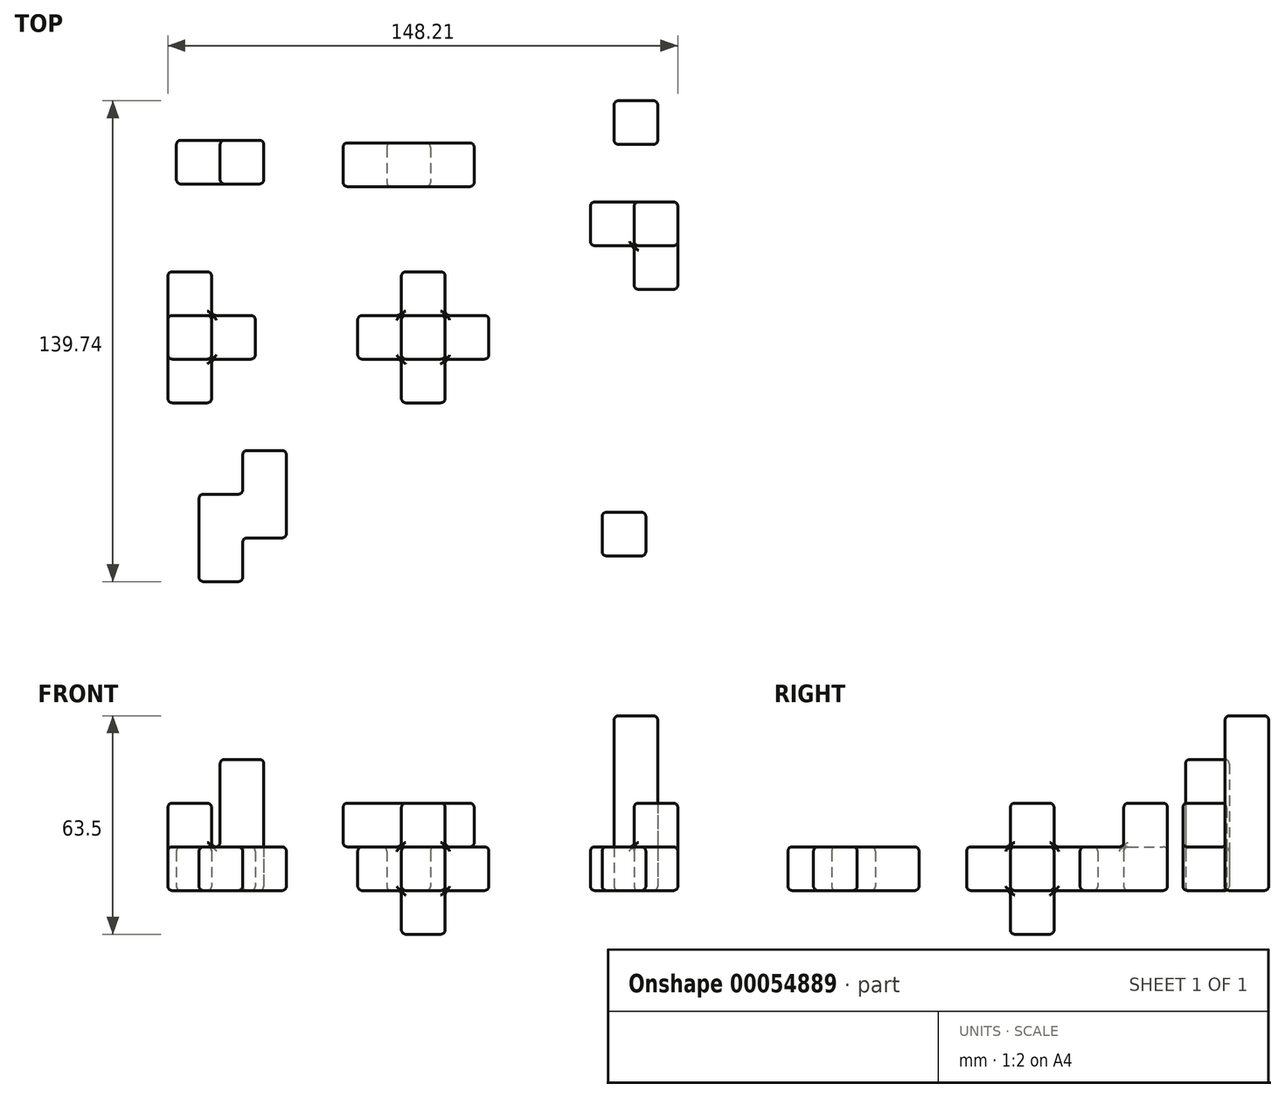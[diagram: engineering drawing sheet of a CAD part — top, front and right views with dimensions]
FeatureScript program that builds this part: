
annotation { "Feature Type Name" : "Feature", "Feature Type Description" : "" }
export const myFeature = defineFeature(function(context is Context, id is Id, definition is map)
    precondition{}
    {
        {
            var Q0;
            Q0=qCreatedBy(makeId("Top.planeOp"),FACE);
            var sketch = newSketch(context, id + "F0", { "sketchPlane" : qUnion([Q0])});
            skLineSegment(sketch, "E0.rect.bottom", {"start": v(6.35, 19.05) * mm, "end": v(-6.35, 19.05) * mm});
            skLineSegment(sketch, "E0.rect.top", {"start": v(6.35, -19.05) * mm, "end": v(-6.35, -19.05) * mm});
            skLineSegment(sketch, "E0.rect.left", {"start": v(6.35, 19.05) * mm, "end": v(6.35, -19.05) * mm});
            skLineSegment(sketch, "E0.rect.right", {"start": v(-6.35, 19.05) * mm, "end": v(-6.35, -19.05) * mm});
            skPoint(sketch, "E0.rect.middle", {"position": v(0, 0) * mm});
            skSolve(sketch);
        }
        {
            var Q0;
            Q0 = qSketchRegion(id + "F0", true);
            extrude(context, id + "F1", {"entities" : qUnion([Q0]), "depth" : 12.7 * mm});
        }
        {
            var Q0;
            Q0=makeQuery(id+"F1.opExtrude","CAP_FACE",FACE,{"disambiguationData":[OSD([sQuery(id+"F0.wireOp",EDGE,"E0.rect.bottom"),sQuery(id+"F0.wireOp",EDGE,"E0.rect.top"),sQuery(id+"F0.wireOp",EDGE,"E0.rect.left"),sQuery(id+"F0.wireOp",EDGE,"E0.rect.right")])],"isStart":false});
            var sketch = newSketch(context, id + "F2", { "sketchPlane" : qUnion([Q0])});
            skLineSegment(sketch, "E1.rect.bottom", {"start": v(6.35, 6.35) * mm, "end": v(-6.35, 6.35) * mm});
            skLineSegment(sketch, "E1.rect.top", {"start": v(6.35, -6.35) * mm, "end": v(-6.35, -6.35) * mm});
            skLineSegment(sketch, "E1.rect.left", {"start": v(6.35, 6.35) * mm, "end": v(6.35, -6.35) * mm});
            skLineSegment(sketch, "E1.rect.right", {"start": v(-6.35, 6.35) * mm, "end": v(-6.35, -6.35) * mm});
            skPoint(sketch, "E1.rect.middle", {"position": v(0, 0) * mm});
            skSolve(sketch);
        }
        {
            var Q0;
            Q0 = qSketchRegion(id + "F2", true);
            extrude(context, id + "F3", {"entities" : qUnion([Q0]), "operationType" : NewBodyOperationType.ADD, "depth" : 12.7 * mm});
        }
        {
            var Q0;
            Q0=makeQuery(id+"F3.boolean.opBoolean","MERGE",FACE,{"derivedFrom":[makeQuery(id+"F1.opExtrude","SWEPT_FACE",FACE,{"disambiguationData":[OSD([sQuery(id+"F0.wireOp",EDGE,"E0.rect.left")])]}),makeQuery(id+"F3.opExtrude","SWEPT_FACE",FACE,{"disambiguationData":[OSD([sQuery(id+"F2.wireOp",EDGE,"E1.rect.left")])]})]});
            var sketch = newSketch(context, id + "F4", { "sketchPlane" : qUnion([Q0])});
            skLineSegment(sketch, "E2.bottom", {"start": v(-6.35, 12.7) * mm, "end": v(6.35, 12.7) * mm});
            skLineSegment(sketch, "E2.top", {"start": v(-6.35, 0) * mm, "end": v(6.35, 0) * mm});
            skLineSegment(sketch, "E2.left", {"start": v(-6.35, 12.7) * mm, "end": v(-6.35, 0) * mm});
            skLineSegment(sketch, "E2.right", {"start": v(6.35, 12.7) * mm, "end": v(6.35, 0) * mm});
            skSolve(sketch);
        }
        {
            var Q0;
            Q0 = qSketchRegion(id + "F4", true);
            extrude(context, id + "F5", {"entities" : qUnion([Q0]), "operationType" : NewBodyOperationType.ADD, "depth" : 12.7 * mm});
        }
        {
            var Q0;
            Q0 = qSketchRegion(id + "F4", true);
            extrude(context, id + "F6", {"entities" : qUnion([Q0]), "operationType" : NewBodyOperationType.ADD, "oppositeDirection" : true, "depth" : 25.4 * mm});
        }
        {
            var Q0;
            Q0 = qSketchRegion(id + "F2", true);
            extrude(context, id + "F7", {"entities" : qUnion([Q0]), "operationType" : NewBodyOperationType.ADD, "oppositeDirection" : true, "depth" : 25.4 * mm});
        }
        {
            var Q0;
            Q0=makeQuery(id+"F1.opExtrude","SWEPT_FACE",FACE,{"disambiguationData":[OSD([sQuery(id+"F0.wireOp",EDGE,"E0.rect.bottom")])]});
            var Q1;
            Q1=makeQuery(id+"F1.opExtrude","SWEPT_EDGE",EDGE,{"disambiguationData":[OSD([sQuery(id+"F0.wireOp",EDGE,"E0.rect.bottom"),sQuery(id+"F0.wireOp",EDGE,"E0.rect.left")])]});
            var Q2;
            Q2=makeQuery(id+"F5.opExtrude","SWEPT_FACE",FACE,{"disambiguationData":[OSD([sQuery(id+"F4.wireOp",EDGE,"E2.bottom")])]});
            var Q3;
            Q3=makeQuery(id+"F1.opExtrude","SWEPT_FACE",FACE,{"disambiguationData":[OSD([sQuery(id+"F0.wireOp",EDGE,"E0.rect.top")])]});
            var Q4;
            Q4=makeQuery(id+"F1.opExtrude","CAP_EDGE",EDGE,{"disambiguationData":[OSD([sQuery(id+"F0.wireOp",EDGE,"E0.rect.bottom")])],"isStart":true});
            var Q5;
            Q5=makeQuery(id+"F3.opExtrude","CAP_EDGE",EDGE,{"disambiguationData":[OSD([sQuery(id+"F2.wireOp",EDGE,"E1.rect.top")])],"isStart":false});
            var Q6;
            Q6=makeQuery(id+"F1.opExtrude","CAP_EDGE",EDGE,{"disambiguationData":[OSD([sQuery(id+"F0.wireOp",EDGE,"E0.rect.bottom")])],"isStart":false});
            var Q7;
            Q7=makeQuery(id+"F1.opExtrude","CAP_EDGE",EDGE,{"disambiguationData":[OSD([sQuery(id+"F0.wireOp",EDGE,"E0.rect.top")])],"isStart":false});
            var Q8;
            Q8=makeQuery(id+"F5.opExtrude","SWEPT_EDGE",EDGE,{"disambiguationData":[OSD([sQuery(id+"F0.wireOp",EDGE,"E0.rect.left"),sQuery(id+"F2.wireOp",EDGE,"E1.rect.bottom"),sQuery(id+"F2.wireOp",EDGE,"E1.rect.left"),sQuery(id+"F4.wireOp",EDGE,"E2.bottom"),sQuery(id+"F4.wireOp",EDGE,"E2.right")])]});
            var Q9;
            Q9=makeQuery(id+"F3.opExtrude","CAP_EDGE",EDGE,{"disambiguationData":[OSD([sQuery(id+"F2.wireOp",EDGE,"E1.rect.bottom")])],"isStart":true});
            var Q10;
            Q10=makeQuery(id+"F7.opExtrude","CAP_EDGE",EDGE,{"disambiguationData":[OSD([sQuery(id+"F2.wireOp",EDGE,"E1.rect.bottom")])],"isStart":false});
            var Q11;
            Q11=makeQuery(id+"F5.opExtrude","SWEPT_EDGE",EDGE,{"disambiguationData":[OSD([sQuery(id+"F0.wireOp",EDGE,"E0.rect.left"),sQuery(id+"F2.wireOp",EDGE,"E1.rect.top"),sQuery(id+"F2.wireOp",EDGE,"E1.rect.left"),sQuery(id+"F4.wireOp",EDGE,"E2.bottom"),sQuery(id+"F4.wireOp",EDGE,"E2.left")])]});
            var Q12;
            {var subQ0=sQuery(id+"F0.wireOp",EDGE,"E0.rect.right");var subQ1=sQuery(id+"F0.wireOp",EDGE,"E0.rect.left");var subQ2=sQuery(id+"F0.wireOp",EDGE,"E0.rect.bottom");Q12=makeQuery(id+"F3.boolean.opBoolean","SPLIT",FACE,{"disambiguationData":[TD([makeQuery(id+"F1.opExtrude","SWEPT_FACE",FACE,{"disambiguationData":[OSD([subQ2])]})])],"derivedFrom":makeQuery(id+"F1.opExtrude","CAP_FACE",FACE,{"disambiguationData":[OSD([subQ2,sQuery(id+"F0.wireOp",EDGE,"E0.rect.top"),subQ1,subQ0])],"isStart":false})});}
            var Q13;
            {var subQ0=sQuery(id+"F0.wireOp",EDGE,"E0.rect.left");var subQ1=sQuery(id+"F0.wireOp",EDGE,"E0.rect.bottom");Q13=makeQuery(id+"F3.boolean.opBoolean","SPLIT",EDGE,{"disambiguationData":[TD([makeQuery(id+"F1.opExtrude","SWEPT_FACE",FACE,{"disambiguationData":[OSD([subQ1])]})])],"derivedFrom":makeQuery(id+"F1.opExtrude","CAP_EDGE",EDGE,{"disambiguationData":[OSD([subQ0])],"isStart":false})});}
            var Q14;
            Q14=makeQuery(id+"F3.opExtrude","CAP_EDGE",EDGE,{"disambiguationData":[OSD([sQuery(id+"F2.wireOp",EDGE,"E1.rect.left")])],"isStart":false});
            var Q15;
            {var subQ0=sQuery(id+"F0.wireOp",EDGE,"E0.rect.right");var subQ1=sQuery(id+"F0.wireOp",EDGE,"E0.rect.left");var subQ2=sQuery(id+"F0.wireOp",EDGE,"E0.rect.top");Q15=makeQuery(id+"F3.boolean.opBoolean","SPLIT",FACE,{"disambiguationData":[TD([makeQuery(id+"F1.opExtrude","SWEPT_FACE",FACE,{"disambiguationData":[OSD([subQ2])]})])],"derivedFrom":makeQuery(id+"F1.opExtrude","CAP_FACE",FACE,{"disambiguationData":[OSD([sQuery(id+"F0.wireOp",EDGE,"E0.rect.bottom"),subQ2,subQ1,subQ0])],"isStart":false})});}
            var Q16;
            {var subQ0=sQuery(id+"F0.wireOp",EDGE,"E0.rect.right");var subQ1=sQuery(id+"F0.wireOp",EDGE,"E0.rect.bottom");Q16=makeQuery(id+"F3.boolean.opBoolean","SPLIT",EDGE,{"disambiguationData":[TD([makeQuery(id+"F1.opExtrude","SWEPT_FACE",FACE,{"disambiguationData":[OSD([subQ1])]})])],"derivedFrom":makeQuery(id+"F1.opExtrude","CAP_EDGE",EDGE,{"disambiguationData":[OSD([subQ0])],"isStart":false})});}
            var Q17;
            Q17=makeQuery(id+"F3.opExtrude","CAP_EDGE",EDGE,{"disambiguationData":[OSD([sQuery(id+"F2.wireOp",EDGE,"E1.rect.right")])],"isStart":false});
            var Q18;
            Q18=makeQuery(id+"F3.opExtrude","SWEPT_FACE",FACE,{"disambiguationData":[OSD([sQuery(id+"F2.wireOp",EDGE,"E1.rect.bottom")])]});
            var Q19;
            Q19=makeQuery(id+"F5.opExtrude","SWEPT_EDGE",EDGE,{"disambiguationData":[OSD([sQuery(id+"F0.wireOp",EDGE,"E0.rect.left"),sQuery(id+"F4.wireOp",EDGE,"E2.top"),sQuery(id+"F4.wireOp",EDGE,"E2.right")])]});
            var Q20;
            Q20=makeQuery(id+"F3.opExtrude","SWEPT_EDGE",EDGE,{"disambiguationData":[OSD([sQuery(id+"F0.wireOp",EDGE,"E0.rect.right"),sQuery(id+"F2.wireOp",EDGE,"E1.rect.bottom"),sQuery(id+"F2.wireOp",EDGE,"E1.rect.right")])]});
            var Q21;
            Q21=makeQuery(id+"F3.opExtrude","CAP_FACE",FACE,{"disambiguationData":[OSD([sQuery(id+"F2.wireOp",EDGE,"E1.rect.bottom"),sQuery(id+"F2.wireOp",EDGE,"E1.rect.top"),sQuery(id+"F2.wireOp",EDGE,"E1.rect.left"),sQuery(id+"F2.wireOp",EDGE,"E1.rect.right")])],"isStart":false});
            var Q22;
            Q22=makeQuery(id+"F3.opExtrude","SWEPT_FACE",FACE,{"disambiguationData":[OSD([sQuery(id+"F2.wireOp",EDGE,"E1.rect.top")])]});
            var Q23;
            Q23=makeQuery(id+"F3.opExtrude","CAP_EDGE",EDGE,{"disambiguationData":[OSD([sQuery(id+"F2.wireOp",EDGE,"E1.rect.bottom")])],"isStart":false});
            var Q24;
            Q24=makeQuery(id+"F5.opExtrude","CAP_FACE",FACE,{"disambiguationData":[OSD([sQuery(id+"F4.wireOp",EDGE,"E2.bottom"),sQuery(id+"F4.wireOp",EDGE,"E2.top"),sQuery(id+"F4.wireOp",EDGE,"E2.left"),sQuery(id+"F4.wireOp",EDGE,"E2.right")])],"isStart":false});
            var Q25;
            Q25=makeQuery(id+"F5.opExtrude","SWEPT_FACE",FACE,{"disambiguationData":[OSD([sQuery(id+"F4.wireOp",EDGE,"E2.left")])]});
            var Q26;
            Q26=makeQuery(id+"F5.opExtrude","CAP_EDGE",EDGE,{"disambiguationData":[OSD([sQuery(id+"F4.wireOp",EDGE,"E2.bottom")])],"isStart":false});
            var Q27;
            Q27=makeQuery(id+"F5.opExtrude","SWEPT_FACE",FACE,{"disambiguationData":[OSD([sQuery(id+"F4.wireOp",EDGE,"E2.right")])]});
            var Q28;
            Q28=makeQuery(id+"F5.opExtrude","CAP_EDGE",EDGE,{"disambiguationData":[OSD([sQuery(id+"F4.wireOp",EDGE,"E2.bottom")])],"isStart":true});
            var Q29;
            Q29=makeQuery(id+"F5.opExtrude","CAP_EDGE",EDGE,{"disambiguationData":[OSD([sQuery(id+"F4.wireOp",EDGE,"E2.top")])],"isStart":false});
            var Q30;
            {var subQ0=sQuery(id+"F2.wireOp",EDGE,"E1.rect.left");var subQ1=sQuery(id+"F2.wireOp",EDGE,"E1.rect.top");var subQ2=sQuery(id+"F2.wireOp",EDGE,"E1.rect.bottom");var subQ3=sQuery(id+"F0.wireOp",EDGE,"E0.rect.left");var subQ4=makeQuery(id+"F1.opExtrude","SWEPT_FACE",FACE,{"disambiguationData":[OSD([subQ3])]});var subQ5=makeQuery(id+"F3.opExtrude","SWEPT_FACE",FACE,{"disambiguationData":[OSD([subQ0])]});Q30=makeQuery(id+"F5.boolean.opBoolean","SPLIT",FACE,{"disambiguationData":[TD([makeQuery(id+"F3.opExtrude","CAP_FACE",FACE,{"disambiguationData":[OSD([subQ2,subQ1,subQ0,sQuery(id+"F2.wireOp",EDGE,"E1.rect.right")])],"isStart":false})])],"derivedFrom":makeQuery(id+"F3.boolean.opBoolean","MERGE",FACE,{"derivedFrom":[subQ4,subQ5]})});}
            var Q31;
            {var subQ0=sQuery(id+"F0.wireOp",EDGE,"E0.rect.left");var subQ1=makeQuery(id+"F1.opExtrude","SWEPT_FACE",FACE,{"disambiguationData":[OSD([subQ0])]});var subQ4=sQuery(id+"F0.wireOp",EDGE,"E0.rect.bottom");var subQ5=makeQuery(id+"F3.opExtrude","SWEPT_FACE",FACE,{"disambiguationData":[OSD([sQuery(id+"F2.wireOp",EDGE,"E1.rect.left")])]});Q31=makeQuery(id+"F5.boolean.opBoolean","SPLIT",FACE,{"disambiguationData":[TD([makeQuery(id+"F1.opExtrude","SWEPT_FACE",FACE,{"disambiguationData":[OSD([subQ4])]})])],"derivedFrom":makeQuery(id+"F3.boolean.opBoolean","MERGE",FACE,{"derivedFrom":[subQ1,subQ5]})});}
            var Q32;
            Q32=makeQuery(id+"F7.opExtrude","CAP_FACE",FACE,{"disambiguationData":[OSD([sQuery(id+"F2.wireOp",EDGE,"E1.rect.bottom"),sQuery(id+"F2.wireOp",EDGE,"E1.rect.top"),sQuery(id+"F2.wireOp",EDGE,"E1.rect.left"),sQuery(id+"F2.wireOp",EDGE,"E1.rect.right")])],"isStart":false});
            var Q33;
            {var subQ0=sQuery(id+"F0.wireOp",EDGE,"E0.rect.left");var subQ1=makeQuery(id+"F1.opExtrude","SWEPT_FACE",FACE,{"disambiguationData":[OSD([subQ0])]});var subQ2=sQuery(id+"F0.wireOp",EDGE,"E0.rect.top");var subQ5=makeQuery(id+"F3.opExtrude","SWEPT_FACE",FACE,{"disambiguationData":[OSD([sQuery(id+"F2.wireOp",EDGE,"E1.rect.left")])]});Q33=makeQuery(id+"F5.boolean.opBoolean","SPLIT",FACE,{"disambiguationData":[TD([makeQuery(id+"F1.opExtrude","SWEPT_FACE",FACE,{"disambiguationData":[OSD([subQ2])]})])],"derivedFrom":makeQuery(id+"F3.boolean.opBoolean","MERGE",FACE,{"derivedFrom":[subQ1,subQ5]})});}
            var Q34;
            {var subQ0=sQuery(id+"F0.wireOp",EDGE,"E0.rect.left");var subQ1=sQuery(id+"F0.wireOp",EDGE,"E0.rect.bottom");Q34=makeQuery(id+"F5.boolean.opBoolean","SPLIT",EDGE,{"disambiguationData":[TD([makeQuery(id+"F1.opExtrude","SWEPT_FACE",FACE,{"disambiguationData":[OSD([subQ1])]})])],"derivedFrom":makeQuery(id+"F1.opExtrude","CAP_EDGE",EDGE,{"disambiguationData":[OSD([subQ0])],"isStart":true})});}
            var Q35;
            {var subQ0=sQuery(id+"F0.wireOp",EDGE,"E0.rect.left");var subQ1=sQuery(id+"F0.wireOp",EDGE,"E0.rect.top");Q35=makeQuery(id+"F5.boolean.opBoolean","SPLIT",EDGE,{"disambiguationData":[TD([makeQuery(id+"F1.opExtrude","SWEPT_FACE",FACE,{"disambiguationData":[OSD([subQ1])]})])],"derivedFrom":makeQuery(id+"F1.opExtrude","CAP_EDGE",EDGE,{"disambiguationData":[OSD([subQ0])],"isStart":true})});}
            var Q36;
            Q36=makeQuery(id+"F6.opExtrude","SWEPT_FACE",FACE,{"disambiguationData":[OSD([sQuery(id+"F4.wireOp",EDGE,"E2.right")])]});
            var Q37;
            Q37=makeQuery(id+"F6.opExtrude","CAP_EDGE",EDGE,{"disambiguationData":[OSD([sQuery(id+"F4.wireOp",EDGE,"E2.right")])],"isStart":false});
            var Q38;
            {var subQ0=sQuery(id+"F0.wireOp",EDGE,"E0.rect.right");var subQ1=makeQuery(id+"F1.opExtrude","SWEPT_FACE",FACE,{"disambiguationData":[OSD([subQ0])]});var subQ4=sQuery(id+"F0.wireOp",EDGE,"E0.rect.bottom");var subQ5=makeQuery(id+"F3.opExtrude","SWEPT_FACE",FACE,{"disambiguationData":[OSD([sQuery(id+"F2.wireOp",EDGE,"E1.rect.right")])]});Q38=makeQuery(id+"F6.boolean.opBoolean","SPLIT",FACE,{"disambiguationData":[TD([makeQuery(id+"F1.opExtrude","SWEPT_FACE",FACE,{"disambiguationData":[OSD([subQ4])]})])],"derivedFrom":makeQuery(id+"F3.boolean.opBoolean","MERGE",FACE,{"derivedFrom":[subQ1,subQ5]})});}
            var Q39;
            Q39=makeQuery(id+"F6.opExtrude","CAP_FACE",FACE,{"disambiguationData":[OSD([sQuery(id+"F4.wireOp",EDGE,"E2.bottom"),sQuery(id+"F4.wireOp",EDGE,"E2.top"),sQuery(id+"F4.wireOp",EDGE,"E2.left"),sQuery(id+"F4.wireOp",EDGE,"E2.right")])],"isStart":false});
            var Q40;
            Q40=makeQuery(id+"F6.opExtrude","SWEPT_EDGE",EDGE,{"disambiguationData":[OSD([sQuery(id+"F0.wireOp",EDGE,"E0.rect.left"),sQuery(id+"F2.wireOp",EDGE,"E1.rect.bottom"),sQuery(id+"F2.wireOp",EDGE,"E1.rect.left"),sQuery(id+"F4.wireOp",EDGE,"E2.bottom"),sQuery(id+"F4.wireOp",EDGE,"E2.right")])]});
            var Q41;
            Q41=makeQuery(id+"F6.opExtrude","SWEPT_FACE",FACE,{"disambiguationData":[OSD([sQuery(id+"F4.wireOp",EDGE,"E2.bottom")])]});
            var Q42;
            Q42=makeQuery(id+"F7.opExtrude","SWEPT_FACE",FACE,{"disambiguationData":[OSD([sQuery(id+"F2.wireOp",EDGE,"E1.rect.bottom")])]});
            var Q43;
            Q43=makeQuery(id+"F7.opExtrude","SWEPT_FACE",FACE,{"disambiguationData":[OSD([sQuery(id+"F2.wireOp",EDGE,"E1.rect.top")])]});
            var Q44;
            Q44=makeQuery(id+"F7.opExtrude","SWEPT_EDGE",EDGE,{"disambiguationData":[OSD([sQuery(id+"F0.wireOp",EDGE,"E0.rect.right"),sQuery(id+"F2.wireOp",EDGE,"E1.rect.bottom"),sQuery(id+"F2.wireOp",EDGE,"E1.rect.right")])]});
            var Q45;
            Q45=makeQuery(id+"F7.opExtrude","SWEPT_FACE",FACE,{"disambiguationData":[OSD([sQuery(id+"F2.wireOp",EDGE,"E1.rect.left")])]});
            var Q46;
            Q46=makeQuery(id+"F7.opExtrude","CAP_EDGE",EDGE,{"disambiguationData":[OSD([sQuery(id+"F2.wireOp",EDGE,"E1.rect.left")])],"isStart":false});
            var Q47;
            {var subQ0=sQuery(id+"F4.wireOp",EDGE,"E2.top");var subQ1=makeQuery(id+"F6.opExtrude","SWEPT_FACE",FACE,{"disambiguationData":[OSD([subQ0])]});var subQ2=makeQuery(id+"F5.opExtrude","SWEPT_FACE",FACE,{"disambiguationData":[OSD([subQ0])]});var subQ4=sQuery(id+"F0.wireOp",EDGE,"E0.rect.left");var subQ5=sQuery(id+"F0.wireOp",EDGE,"E0.rect.bottom");var subQ7=sQuery(id+"F0.wireOp",EDGE,"E0.rect.right");var subQ8=makeQuery(id+"F1.opExtrude","CAP_FACE",FACE,{"disambiguationData":[OSD([subQ5,sQuery(id+"F0.wireOp",EDGE,"E0.rect.top"),subQ4,subQ7])],"isStart":true});Q47=makeQuery(id+"F7.boolean.opBoolean","SPLIT",FACE,{"disambiguationData":[TD([makeQuery(id+"F1.opExtrude","SWEPT_FACE",FACE,{"disambiguationData":[OSD([subQ5])]})])],"derivedFrom":makeQuery(id+"F6.boolean.opBoolean","MERGE",FACE,{"derivedFrom":[makeQuery(id+"F5.boolean.opBoolean","MERGE",FACE,{"derivedFrom":[subQ8,subQ2]}),subQ1]})});}
            var Q48;
            Q48=makeQuery(id+"F1.opExtrude","SWEPT_EDGE",EDGE,{"disambiguationData":[OSD([sQuery(id+"F0.wireOp",EDGE,"E0.rect.bottom"),sQuery(id+"F0.wireOp",EDGE,"E0.rect.right")])]});
            var Q49;
            Q49=makeQuery(id+"F1.opExtrude","SWEPT_EDGE",EDGE,{"disambiguationData":[OSD([sQuery(id+"F0.wireOp",EDGE,"E0.rect.top"),sQuery(id+"F0.wireOp",EDGE,"E0.rect.left")])]});
            var Q50;
            Q50=makeQuery(id+"F1.opExtrude","SWEPT_EDGE",EDGE,{"disambiguationData":[OSD([sQuery(id+"F0.wireOp",EDGE,"E0.rect.top"),sQuery(id+"F0.wireOp",EDGE,"E0.rect.right")])]});
            var Q51;
            Q51=makeQuery(id+"F1.opExtrude","CAP_EDGE",EDGE,{"disambiguationData":[OSD([sQuery(id+"F0.wireOp",EDGE,"E0.rect.top")])],"isStart":true});
            var Q52;
            Q52=makeQuery(id+"F6.opExtrude","SWEPT_EDGE",EDGE,{"disambiguationData":[OSD([sQuery(id+"F0.wireOp",EDGE,"E0.rect.left"),sQuery(id+"F4.wireOp",EDGE,"E2.top"),sQuery(id+"F4.wireOp",EDGE,"E2.right")])]});
            var Q53;
            Q53=makeQuery(id+"F3.opExtrude","CAP_EDGE",EDGE,{"disambiguationData":[OSD([sQuery(id+"F2.wireOp",EDGE,"E1.rect.top")])],"isStart":true});
            var Q54;
            Q54=makeQuery(id+"F6.opExtrude","SWEPT_FACE",FACE,{"disambiguationData":[OSD([sQuery(id+"F4.wireOp",EDGE,"E2.left")])]});
            var Q55;
            {var subQ0=sQuery(id+"F0.wireOp",EDGE,"E0.rect.left");var subQ1=sQuery(id+"F0.wireOp",EDGE,"E0.rect.top");Q55=makeQuery(id+"F3.boolean.opBoolean","SPLIT",EDGE,{"disambiguationData":[TD([makeQuery(id+"F1.opExtrude","SWEPT_FACE",FACE,{"disambiguationData":[OSD([subQ1])]})])],"derivedFrom":makeQuery(id+"F1.opExtrude","CAP_EDGE",EDGE,{"disambiguationData":[OSD([subQ0])],"isStart":false})});}
            var Q56;
            {var subQ0=sQuery(id+"F0.wireOp",EDGE,"E0.rect.right");var subQ1=sQuery(id+"F0.wireOp",EDGE,"E0.rect.top");Q56=makeQuery(id+"F3.boolean.opBoolean","SPLIT",EDGE,{"disambiguationData":[TD([makeQuery(id+"F1.opExtrude","SWEPT_FACE",FACE,{"disambiguationData":[OSD([subQ1])]})])],"derivedFrom":makeQuery(id+"F1.opExtrude","CAP_EDGE",EDGE,{"disambiguationData":[OSD([subQ0])],"isStart":false})});}
            var Q57;
            Q57=makeQuery(id+"F3.opExtrude","SWEPT_EDGE",EDGE,{"disambiguationData":[OSD([sQuery(id+"F0.wireOp",EDGE,"E0.rect.left"),sQuery(id+"F2.wireOp",EDGE,"E1.rect.bottom"),sQuery(id+"F2.wireOp",EDGE,"E1.rect.left")])]});
            var Q58;
            Q58=makeQuery(id+"F3.opExtrude","SWEPT_EDGE",EDGE,{"disambiguationData":[OSD([sQuery(id+"F0.wireOp",EDGE,"E0.rect.left"),sQuery(id+"F2.wireOp",EDGE,"E1.rect.top"),sQuery(id+"F2.wireOp",EDGE,"E1.rect.left")])]});
            var Q59;
            Q59=makeQuery(id+"F3.opExtrude","SWEPT_EDGE",EDGE,{"disambiguationData":[OSD([sQuery(id+"F0.wireOp",EDGE,"E0.rect.right"),sQuery(id+"F2.wireOp",EDGE,"E1.rect.top"),sQuery(id+"F2.wireOp",EDGE,"E1.rect.right")])]});
            var Q60;
            Q60=makeQuery(id+"F5.opExtrude","SWEPT_EDGE",EDGE,{"disambiguationData":[OSD([sQuery(id+"F0.wireOp",EDGE,"E0.rect.left"),sQuery(id+"F4.wireOp",EDGE,"E2.top"),sQuery(id+"F4.wireOp",EDGE,"E2.left")])]});
            var Q61;
            Q61=makeQuery(id+"F5.opExtrude","CAP_EDGE",EDGE,{"disambiguationData":[OSD([sQuery(id+"F4.wireOp",EDGE,"E2.left")])],"isStart":true});
            var Q62;
            Q62=makeQuery(id+"F5.opExtrude","CAP_EDGE",EDGE,{"disambiguationData":[OSD([sQuery(id+"F4.wireOp",EDGE,"E2.right")])],"isStart":true});
            var Q63;
            Q63=makeQuery(id+"F5.opExtrude","CAP_EDGE",EDGE,{"disambiguationData":[OSD([sQuery(id+"F4.wireOp",EDGE,"E2.left")])],"isStart":false});
            var Q64;
            Q64=makeQuery(id+"F5.opExtrude","CAP_EDGE",EDGE,{"disambiguationData":[OSD([sQuery(id+"F4.wireOp",EDGE,"E2.right")])],"isStart":false});
            var Q65;
            Q65=makeQuery(id+"F6.opExtrude","SWEPT_EDGE",EDGE,{"disambiguationData":[OSD([sQuery(id+"F0.wireOp",EDGE,"E0.rect.left"),sQuery(id+"F4.wireOp",EDGE,"E2.top"),sQuery(id+"F4.wireOp",EDGE,"E2.left")])]});
            var Q66;
            {var subQ0=sQuery(id+"F2.wireOp",EDGE,"E1.rect.right");var subQ1=sQuery(id+"F2.wireOp",EDGE,"E1.rect.top");var subQ2=sQuery(id+"F2.wireOp",EDGE,"E1.rect.bottom");var subQ3=sQuery(id+"F0.wireOp",EDGE,"E0.rect.right");var subQ4=makeQuery(id+"F1.opExtrude","SWEPT_FACE",FACE,{"disambiguationData":[OSD([subQ3])]});var subQ5=makeQuery(id+"F3.opExtrude","SWEPT_FACE",FACE,{"disambiguationData":[OSD([subQ0])]});Q66=makeQuery(id+"F6.boolean.opBoolean","SPLIT",FACE,{"disambiguationData":[TD([makeQuery(id+"F3.opExtrude","CAP_FACE",FACE,{"disambiguationData":[OSD([subQ2,subQ1,sQuery(id+"F2.wireOp",EDGE,"E1.rect.left"),subQ0])],"isStart":false})])],"derivedFrom":makeQuery(id+"F3.boolean.opBoolean","MERGE",FACE,{"derivedFrom":[subQ4,subQ5]})});}
            var Q67;
            Q67=makeQuery(id+"F6.boolean.opBoolean","INTERSECT",EDGE,{"derivedFrom":[makeQuery(id+"F3.boolean.opBoolean","MERGE",FACE,{"derivedFrom":[makeQuery(id+"F1.opExtrude","SWEPT_FACE",FACE,{"disambiguationData":[OSD([sQuery(id+"F0.wireOp",EDGE,"E0.rect.right")])]}),makeQuery(id+"F3.opExtrude","SWEPT_FACE",FACE,{"disambiguationData":[OSD([sQuery(id+"F2.wireOp",EDGE,"E1.rect.right")])]})]}),makeQuery(id+"F6.opExtrude","SWEPT_FACE",FACE,{"disambiguationData":[OSD([sQuery(id+"F4.wireOp",EDGE,"E2.bottom")])]})]});
            var Q68;
            Q68=makeQuery(id+"F6.boolean.opBoolean","INTERSECT",EDGE,{"derivedFrom":[makeQuery(id+"F3.boolean.opBoolean","MERGE",FACE,{"derivedFrom":[makeQuery(id+"F1.opExtrude","SWEPT_FACE",FACE,{"disambiguationData":[OSD([sQuery(id+"F0.wireOp",EDGE,"E0.rect.right")])]}),makeQuery(id+"F3.opExtrude","SWEPT_FACE",FACE,{"disambiguationData":[OSD([sQuery(id+"F2.wireOp",EDGE,"E1.rect.right")])]})]}),makeQuery(id+"F6.opExtrude","SWEPT_FACE",FACE,{"disambiguationData":[OSD([sQuery(id+"F4.wireOp",EDGE,"E2.right")])]})]});
            var Q69;
            {var subQ0=sQuery(id+"F0.wireOp",EDGE,"E0.rect.right");var subQ1=makeQuery(id+"F1.opExtrude","SWEPT_FACE",FACE,{"disambiguationData":[OSD([subQ0])]});var subQ2=sQuery(id+"F0.wireOp",EDGE,"E0.rect.top");var subQ5=makeQuery(id+"F3.opExtrude","SWEPT_FACE",FACE,{"disambiguationData":[OSD([sQuery(id+"F2.wireOp",EDGE,"E1.rect.right")])]});Q69=makeQuery(id+"F6.boolean.opBoolean","SPLIT",FACE,{"disambiguationData":[TD([makeQuery(id+"F1.opExtrude","SWEPT_FACE",FACE,{"disambiguationData":[OSD([subQ2])]})])],"derivedFrom":makeQuery(id+"F3.boolean.opBoolean","MERGE",FACE,{"derivedFrom":[subQ1,subQ5]})});}
            var Q70;
            {var subQ0=sQuery(id+"F0.wireOp",EDGE,"E0.rect.right");var subQ1=sQuery(id+"F0.wireOp",EDGE,"E0.rect.bottom");Q70=makeQuery(id+"F6.boolean.opBoolean","SPLIT",EDGE,{"disambiguationData":[TD([makeQuery(id+"F1.opExtrude","SWEPT_FACE",FACE,{"disambiguationData":[OSD([subQ1])]})])],"derivedFrom":makeQuery(id+"F1.opExtrude","CAP_EDGE",EDGE,{"disambiguationData":[OSD([subQ0])],"isStart":true})});}
            var Q71;
            {var subQ0=sQuery(id+"F0.wireOp",EDGE,"E0.rect.right");var subQ1=sQuery(id+"F0.wireOp",EDGE,"E0.rect.top");Q71=makeQuery(id+"F6.boolean.opBoolean","SPLIT",EDGE,{"disambiguationData":[TD([makeQuery(id+"F1.opExtrude","SWEPT_FACE",FACE,{"disambiguationData":[OSD([subQ1])]})])],"derivedFrom":makeQuery(id+"F1.opExtrude","CAP_EDGE",EDGE,{"disambiguationData":[OSD([subQ0])],"isStart":true})});}
            var Q72;
            Q72=makeQuery(id+"F6.opExtrude","CAP_EDGE",EDGE,{"disambiguationData":[OSD([sQuery(id+"F4.wireOp",EDGE,"E2.bottom")])],"isStart":false});
            var Q73;
            Q73=makeQuery(id+"F6.opExtrude","CAP_EDGE",EDGE,{"disambiguationData":[OSD([sQuery(id+"F4.wireOp",EDGE,"E2.top")])],"isStart":false});
            var Q74;
            Q74=makeQuery(id+"F7.opExtrude","SWEPT_EDGE",EDGE,{"disambiguationData":[OSD([sQuery(id+"F0.wireOp",EDGE,"E0.rect.left"),sQuery(id+"F2.wireOp",EDGE,"E1.rect.bottom"),sQuery(id+"F2.wireOp",EDGE,"E1.rect.left")])]});
            var Q75;
            Q75=makeQuery(id+"F7.opExtrude","CAP_EDGE",EDGE,{"disambiguationData":[OSD([sQuery(id+"F2.wireOp",EDGE,"E1.rect.top")])],"isStart":false});
            var Q76;
            Q76=makeQuery(id+"F7.opExtrude","SWEPT_EDGE",EDGE,{"disambiguationData":[OSD([sQuery(id+"F0.wireOp",EDGE,"E0.rect.left"),sQuery(id+"F2.wireOp",EDGE,"E1.rect.top"),sQuery(id+"F2.wireOp",EDGE,"E1.rect.left")])]});
            var Q77;
            Q77=makeQuery(id+"F7.opExtrude","SWEPT_FACE",FACE,{"disambiguationData":[OSD([sQuery(id+"F2.wireOp",EDGE,"E1.rect.right")])]});
            var Q78;
            Q78=makeQuery(id+"F7.opExtrude","SWEPT_EDGE",EDGE,{"disambiguationData":[OSD([sQuery(id+"F0.wireOp",EDGE,"E0.rect.right"),sQuery(id+"F2.wireOp",EDGE,"E1.rect.top"),sQuery(id+"F2.wireOp",EDGE,"E1.rect.right")])]});
            var Q79;
            {var subQ0=sQuery(id+"F4.wireOp",EDGE,"E2.top");var subQ1=makeQuery(id+"F6.opExtrude","SWEPT_FACE",FACE,{"disambiguationData":[OSD([subQ0])]});var subQ2=sQuery(id+"F0.wireOp",EDGE,"E0.rect.top");var subQ4=makeQuery(id+"F5.opExtrude","SWEPT_FACE",FACE,{"disambiguationData":[OSD([subQ0])]});var subQ6=sQuery(id+"F0.wireOp",EDGE,"E0.rect.left");var subQ8=sQuery(id+"F0.wireOp",EDGE,"E0.rect.right");var subQ9=makeQuery(id+"F1.opExtrude","CAP_FACE",FACE,{"disambiguationData":[OSD([sQuery(id+"F0.wireOp",EDGE,"E0.rect.bottom"),subQ2,subQ6,subQ8])],"isStart":true});Q79=makeQuery(id+"F7.boolean.opBoolean","SPLIT",FACE,{"disambiguationData":[TD([makeQuery(id+"F1.opExtrude","SWEPT_FACE",FACE,{"disambiguationData":[OSD([subQ2])]})])],"derivedFrom":makeQuery(id+"F6.boolean.opBoolean","MERGE",FACE,{"derivedFrom":[makeQuery(id+"F5.boolean.opBoolean","MERGE",FACE,{"derivedFrom":[subQ9,subQ4]}),subQ1]})});}
            var Q80;
            {var subQ0=sQuery(id+"F4.wireOp",EDGE,"E2.top");Q80=makeQuery(id+"F7.boolean.opBoolean","INTERSECT",EDGE,{"derivedFrom":[makeQuery(id+"F6.boolean.opBoolean","MERGE",FACE,{"derivedFrom":[makeQuery(id+"F5.boolean.opBoolean","MERGE",FACE,{"derivedFrom":[makeQuery(id+"F1.opExtrude","CAP_FACE",FACE,{"disambiguationData":[OSD([sQuery(id+"F0.wireOp",EDGE,"E0.rect.bottom"),sQuery(id+"F0.wireOp",EDGE,"E0.rect.top"),sQuery(id+"F0.wireOp",EDGE,"E0.rect.left"),sQuery(id+"F0.wireOp",EDGE,"E0.rect.right")])],"isStart":true}),makeQuery(id+"F5.opExtrude","SWEPT_FACE",FACE,{"disambiguationData":[OSD([subQ0])]})]}),makeQuery(id+"F6.opExtrude","SWEPT_FACE",FACE,{"disambiguationData":[OSD([subQ0])]})]}),makeQuery(id+"F7.opExtrude","SWEPT_FACE",FACE,{"disambiguationData":[OSD([sQuery(id+"F2.wireOp",EDGE,"E1.rect.bottom")])]})]});}
            var Q81;
            {var subQ0=sQuery(id+"F4.wireOp",EDGE,"E2.top");Q81=makeQuery(id+"F7.boolean.opBoolean","INTERSECT",EDGE,{"derivedFrom":[makeQuery(id+"F6.boolean.opBoolean","MERGE",FACE,{"derivedFrom":[makeQuery(id+"F5.boolean.opBoolean","MERGE",FACE,{"derivedFrom":[makeQuery(id+"F1.opExtrude","CAP_FACE",FACE,{"disambiguationData":[OSD([sQuery(id+"F0.wireOp",EDGE,"E0.rect.bottom"),sQuery(id+"F0.wireOp",EDGE,"E0.rect.top"),sQuery(id+"F0.wireOp",EDGE,"E0.rect.left"),sQuery(id+"F0.wireOp",EDGE,"E0.rect.right")])],"isStart":true}),makeQuery(id+"F5.opExtrude","SWEPT_FACE",FACE,{"disambiguationData":[OSD([subQ0])]})]}),makeQuery(id+"F6.opExtrude","SWEPT_FACE",FACE,{"disambiguationData":[OSD([subQ0])]})]}),makeQuery(id+"F7.opExtrude","SWEPT_FACE",FACE,{"disambiguationData":[OSD([sQuery(id+"F2.wireOp",EDGE,"E1.rect.top")])]})]});}
            var Q82;
            {var subQ0=sQuery(id+"F4.wireOp",EDGE,"E2.top");var subQ1=makeQuery(id+"F6.opExtrude","SWEPT_FACE",FACE,{"disambiguationData":[OSD([subQ0])]});var subQ2=sQuery(id+"F4.wireOp",EDGE,"E2.left");var subQ3=makeQuery(id+"F5.opExtrude","SWEPT_FACE",FACE,{"disambiguationData":[OSD([subQ0])]});var subQ4=sQuery(id+"F0.wireOp",EDGE,"E0.rect.left");var subQ5=makeQuery(id+"F1.opExtrude","CAP_FACE",FACE,{"disambiguationData":[OSD([sQuery(id+"F0.wireOp",EDGE,"E0.rect.bottom"),sQuery(id+"F0.wireOp",EDGE,"E0.rect.top"),subQ4,sQuery(id+"F0.wireOp",EDGE,"E0.rect.right")])],"isStart":true});var subQ7=sQuery(id+"F4.wireOp",EDGE,"E2.right");Q82=makeQuery(id+"F7.boolean.opBoolean","SPLIT",FACE,{"disambiguationData":[TD([makeQuery(id+"F5.opExtrude","CAP_FACE",FACE,{"disambiguationData":[OSD([sQuery(id+"F4.wireOp",EDGE,"E2.bottom"),subQ0,subQ2,subQ7])],"isStart":false})])],"derivedFrom":makeQuery(id+"F6.boolean.opBoolean","MERGE",FACE,{"derivedFrom":[makeQuery(id+"F5.boolean.opBoolean","MERGE",FACE,{"derivedFrom":[subQ5,subQ3]}),subQ1]})});}
            var Q83;
            {var subQ0=sQuery(id+"F4.wireOp",EDGE,"E2.right");var subQ1=sQuery(id+"F4.wireOp",EDGE,"E2.top");var subQ2=makeQuery(id+"F6.opExtrude","SWEPT_FACE",FACE,{"disambiguationData":[OSD([subQ1])]});var subQ3=sQuery(id+"F4.wireOp",EDGE,"E2.left");var subQ5=sQuery(id+"F0.wireOp",EDGE,"E0.rect.right");var subQ6=makeQuery(id+"F1.opExtrude","CAP_FACE",FACE,{"disambiguationData":[OSD([sQuery(id+"F0.wireOp",EDGE,"E0.rect.bottom"),sQuery(id+"F0.wireOp",EDGE,"E0.rect.top"),sQuery(id+"F0.wireOp",EDGE,"E0.rect.left"),subQ5])],"isStart":true});var subQ7=makeQuery(id+"F5.opExtrude","SWEPT_FACE",FACE,{"disambiguationData":[OSD([subQ1])]});Q83=makeQuery(id+"F7.boolean.opBoolean","SPLIT",FACE,{"disambiguationData":[TD([makeQuery(id+"F6.opExtrude","CAP_FACE",FACE,{"disambiguationData":[OSD([sQuery(id+"F4.wireOp",EDGE,"E2.bottom"),subQ1,subQ3,subQ0])],"isStart":false})])],"derivedFrom":makeQuery(id+"F6.boolean.opBoolean","MERGE",FACE,{"derivedFrom":[makeQuery(id+"F5.boolean.opBoolean","MERGE",FACE,{"derivedFrom":[subQ6,subQ7]}),subQ2]})});}
            var Q84;
            {var subQ0=sQuery(id+"F4.wireOp",EDGE,"E2.top");Q84=makeQuery(id+"F7.boolean.opBoolean","INTERSECT",EDGE,{"derivedFrom":[makeQuery(id+"F6.boolean.opBoolean","MERGE",FACE,{"derivedFrom":[makeQuery(id+"F5.boolean.opBoolean","MERGE",FACE,{"derivedFrom":[makeQuery(id+"F1.opExtrude","CAP_FACE",FACE,{"disambiguationData":[OSD([sQuery(id+"F0.wireOp",EDGE,"E0.rect.bottom"),sQuery(id+"F0.wireOp",EDGE,"E0.rect.top"),sQuery(id+"F0.wireOp",EDGE,"E0.rect.left"),sQuery(id+"F0.wireOp",EDGE,"E0.rect.right")])],"isStart":true}),makeQuery(id+"F5.opExtrude","SWEPT_FACE",FACE,{"disambiguationData":[OSD([subQ0])]})]}),makeQuery(id+"F6.opExtrude","SWEPT_FACE",FACE,{"disambiguationData":[OSD([subQ0])]})]}),makeQuery(id+"F7.opExtrude","SWEPT_FACE",FACE,{"disambiguationData":[OSD([sQuery(id+"F2.wireOp",EDGE,"E1.rect.right")])]})]});}
            var Q85;
            Q85=makeQuery(id+"F6.opExtrude","CAP_EDGE",EDGE,{"disambiguationData":[OSD([sQuery(id+"F4.wireOp",EDGE,"E2.left")])],"isStart":false});
            var Q86;
            Q86=makeQuery(id+"F6.boolean.opBoolean","INTERSECT",EDGE,{"derivedFrom":[makeQuery(id+"F3.boolean.opBoolean","MERGE",FACE,{"derivedFrom":[makeQuery(id+"F1.opExtrude","SWEPT_FACE",FACE,{"disambiguationData":[OSD([sQuery(id+"F0.wireOp",EDGE,"E0.rect.right")])]}),makeQuery(id+"F3.opExtrude","SWEPT_FACE",FACE,{"disambiguationData":[OSD([sQuery(id+"F2.wireOp",EDGE,"E1.rect.right")])]})]}),makeQuery(id+"F6.opExtrude","SWEPT_FACE",FACE,{"disambiguationData":[OSD([sQuery(id+"F4.wireOp",EDGE,"E2.left")])]})]});
            var Q87;
            Q87=makeQuery(id+"F6.opExtrude","SWEPT_EDGE",EDGE,{"disambiguationData":[OSD([sQuery(id+"F0.wireOp",EDGE,"E0.rect.left"),sQuery(id+"F2.wireOp",EDGE,"E1.rect.top"),sQuery(id+"F2.wireOp",EDGE,"E1.rect.left"),sQuery(id+"F4.wireOp",EDGE,"E2.bottom"),sQuery(id+"F4.wireOp",EDGE,"E2.left")])]});
            var Q88;
            {var subQ0=sQuery(id+"F4.wireOp",EDGE,"E2.top");Q88=makeQuery(id+"F7.boolean.opBoolean","INTERSECT",EDGE,{"derivedFrom":[makeQuery(id+"F6.boolean.opBoolean","MERGE",FACE,{"derivedFrom":[makeQuery(id+"F5.boolean.opBoolean","MERGE",FACE,{"derivedFrom":[makeQuery(id+"F1.opExtrude","CAP_FACE",FACE,{"disambiguationData":[OSD([sQuery(id+"F0.wireOp",EDGE,"E0.rect.bottom"),sQuery(id+"F0.wireOp",EDGE,"E0.rect.top"),sQuery(id+"F0.wireOp",EDGE,"E0.rect.left"),sQuery(id+"F0.wireOp",EDGE,"E0.rect.right")])],"isStart":true}),makeQuery(id+"F5.opExtrude","SWEPT_FACE",FACE,{"disambiguationData":[OSD([subQ0])]})]}),makeQuery(id+"F6.opExtrude","SWEPT_FACE",FACE,{"disambiguationData":[OSD([subQ0])]})]}),makeQuery(id+"F7.opExtrude","SWEPT_FACE",FACE,{"disambiguationData":[OSD([sQuery(id+"F2.wireOp",EDGE,"E1.rect.left")])]})]});}
            var Q89;
            Q89=makeQuery(id+"F7.opExtrude","CAP_EDGE",EDGE,{"disambiguationData":[OSD([sQuery(id+"F2.wireOp",EDGE,"E1.rect.right")])],"isStart":false});
            fillet(context, id + "F8", {"entities" : qUnion([Q0, Q1, Q2, Q3, Q4, Q5, Q6, Q7, Q8, Q9, Q10, Q11, Q12, Q13, Q14, Q15, Q16, Q17, Q18, Q19, Q20, Q21, Q22, Q23, Q24, Q25, Q26, Q27, Q28, Q29, Q30, Q31, Q32, Q33, Q34, Q35, Q36, Q37, Q38, Q39, Q40, Q41, Q42, Q43, Q44, Q45, Q46, Q47, Q48, Q49, Q50, Q51, Q52, Q53, Q54, Q55, Q56, Q57, Q58, Q59, Q60, Q61, Q62, Q63, Q64, Q65, Q66, Q67, Q68, Q69, Q70, Q71, Q72, Q73, Q74, Q75, Q76, Q77, Q78, Q79, Q80, Q81, Q82, Q83, Q84, Q85, Q86, Q87, Q88, Q89]), "radius" : 1.27 * mm, "tangentPropagation" : true, "allowEdgeOverflow" : false});
        }
        {
            var Q0;
            Q0=qCreatedBy(makeId("Top.planeOp"),FACE);
            var sketch = newSketch(context, id + "F9", { "sketchPlane" : qUnion([Q0])});
            skLineSegment(sketch, "E3.bottom", {"start": v(73.96, 13.93) * mm, "end": v(61.26, 13.93) * mm});
            skLineSegment(sketch, "E3.top", {"start": v(73.96, 39.33) * mm, "end": v(61.26, 39.33) * mm});
            skLineSegment(sketch, "E3.left", {"start": v(73.96, 13.93) * mm, "end": v(73.96, 39.33) * mm});
            skLineSegment(sketch, "E3.right", {"start": v(61.26, 13.93) * mm, "end": v(61.26, 39.33) * mm});
            skSolve(sketch);
        }
        {
            var Q0;
            Q0 = qSketchRegion(id + "F9", true);
            extrude(context, id + "F10", {"entities" : qUnion([Q0]), "depth" : 12.7 * mm});
        }
        {
            var Q0;
            Q0=makeQuery(id+"F10.opExtrude","SWEPT_FACE",FACE,{"disambiguationData":[OSD([sQuery(id+"F9.wireOp",EDGE,"E3.right")])]});
            var sketch = newSketch(context, id + "F11", { "sketchPlane" : qUnion([Q0])});
            skLineSegment(sketch, "E4.bottom", {"start": v(-26.63, 12.7) * mm, "end": v(-39.33, 12.7) * mm});
            skLineSegment(sketch, "E4.top", {"start": v(-26.63, 0) * mm, "end": v(-39.33, 0) * mm});
            skLineSegment(sketch, "E4.left", {"start": v(-26.63, 12.7) * mm, "end": v(-26.63, 0) * mm});
            skLineSegment(sketch, "E4.right", {"start": v(-39.33, 12.7) * mm, "end": v(-39.33, 0) * mm});
            skSolve(sketch);
        }
        {
            var Q0;
            Q0 = qSketchRegion(id + "F11", true);
            extrude(context, id + "F12", {"entities" : qUnion([Q0]), "operationType" : NewBodyOperationType.ADD, "depth" : 12.7 * mm});
        }
        {
            var Q0;
            Q0=makeQuery(id+"F12.boolean.opBoolean","MERGE",FACE,{"derivedFrom":[makeQuery(id+"F10.opExtrude","CAP_FACE",FACE,{"disambiguationData":[OSD([sQuery(id+"F9.wireOp",EDGE,"E3.bottom"),sQuery(id+"F9.wireOp",EDGE,"E3.top"),sQuery(id+"F9.wireOp",EDGE,"E3.left"),sQuery(id+"F9.wireOp",EDGE,"E3.right")])],"isStart":false}),makeQuery(id+"F12.opExtrude","SWEPT_FACE",FACE,{"disambiguationData":[OSD([sQuery(id+"F11.wireOp",EDGE,"E4.bottom")])]})]});
            var sketch = newSketch(context, id + "F13", { "sketchPlane" : qUnion([Q0])});
            skLineSegment(sketch, "E5.bottom", {"start": v(61.26, 26.63) * mm, "end": v(73.96, 26.63) * mm});
            skLineSegment(sketch, "E5.top", {"start": v(61.26, 39.33) * mm, "end": v(73.96, 39.33) * mm});
            skLineSegment(sketch, "E5.left", {"start": v(61.26, 26.63) * mm, "end": v(61.26, 39.33) * mm});
            skLineSegment(sketch, "E5.right", {"start": v(73.96, 26.63) * mm, "end": v(73.96, 39.33) * mm});
            skSolve(sketch);
        }
        {
            var Q0;
            Q0 = qSketchRegion(id + "F13", true);
            extrude(context, id + "F14", {"entities" : qUnion([Q0]), "operationType" : NewBodyOperationType.ADD, "depth" : 12.7 * mm});
        }
        {
            var Q0;
            Q0=makeQuery(id+"F12.opExtrude","CAP_EDGE",EDGE,{"disambiguationData":[OSD([sQuery(id+"F11.wireOp",EDGE,"E4.bottom")])],"isStart":false});
            var Q1;
            Q1=makeQuery(id+"F14.opExtrude","CAP_FACE",FACE,{"disambiguationData":[OSD([sQuery(id+"F13.wireOp",EDGE,"E5.bottom"),sQuery(id+"F13.wireOp",EDGE,"E5.top"),sQuery(id+"F13.wireOp",EDGE,"E5.left"),sQuery(id+"F13.wireOp",EDGE,"E5.right")])],"isStart":false});
            var Q2;
            Q2=makeQuery(id+"F12.opExtrude","SWEPT_FACE",FACE,{"disambiguationData":[OSD([sQuery(id+"F11.wireOp",EDGE,"E4.left")])]});
            var Q3;
            Q3=makeQuery(id+"F12.opExtrude","CAP_FACE",FACE,{"disambiguationData":[OSD([sQuery(id+"F11.wireOp",EDGE,"E4.bottom"),sQuery(id+"F11.wireOp",EDGE,"E4.top"),sQuery(id+"F11.wireOp",EDGE,"E4.left"),sQuery(id+"F11.wireOp",EDGE,"E4.right")])],"isStart":false});
            var Q4;
            Q4=makeQuery(id+"F12.opExtrude","SWEPT_EDGE",EDGE,{"disambiguationData":[OSD([sQuery(id+"F9.wireOp",EDGE,"E3.right"),sQuery(id+"F11.wireOp",EDGE,"E4.bottom"),sQuery(id+"F11.wireOp",EDGE,"E4.left")])]});
            var Q5;
            Q5=makeQuery(id+"F10.opExtrude","SWEPT_FACE",FACE,{"disambiguationData":[OSD([sQuery(id+"F9.wireOp",EDGE,"E3.bottom")])]});
            var Q6;
            Q6=makeQuery(id+"F12.boolean.opBoolean","MERGE",EDGE,{"derivedFrom":[makeQuery(id+"F10.opExtrude","CAP_EDGE",EDGE,{"disambiguationData":[OSD([sQuery(id+"F9.wireOp",EDGE,"E3.top")])],"isStart":true}),makeQuery(id+"F12.opExtrude","SWEPT_EDGE",EDGE,{"disambiguationData":[OSD([sQuery(id+"F11.wireOp",EDGE,"E4.top"),sQuery(id+"F11.wireOp",EDGE,"E4.right")])]})]});
            var Q7;
            Q7=makeQuery(id+"F10.opExtrude","SWEPT_EDGE",EDGE,{"disambiguationData":[OSD([sQuery(id+"F9.wireOp",EDGE,"E3.bottom"),sQuery(id+"F9.wireOp",EDGE,"E3.right")])]});
            var Q8;
            Q8=makeQuery(id+"F12.boolean.opBoolean","MERGE",FACE,{"derivedFrom":[makeQuery(id+"F10.opExtrude","CAP_FACE",FACE,{"disambiguationData":[OSD([sQuery(id+"F9.wireOp",EDGE,"E3.bottom"),sQuery(id+"F9.wireOp",EDGE,"E3.top"),sQuery(id+"F9.wireOp",EDGE,"E3.left"),sQuery(id+"F9.wireOp",EDGE,"E3.right")])],"isStart":true}),makeQuery(id+"F12.opExtrude","SWEPT_FACE",FACE,{"disambiguationData":[OSD([sQuery(id+"F11.wireOp",EDGE,"E4.top")])]})]});
            var Q9;
            Q9=makeQuery(id+"F14.opExtrude","SWEPT_EDGE",EDGE,{"disambiguationData":[OSD([sQuery(id+"F9.wireOp",EDGE,"E3.top"),sQuery(id+"F11.wireOp",EDGE,"E4.bottom"),sQuery(id+"F11.wireOp",EDGE,"E4.right"),sQuery(id+"F13.wireOp",EDGE,"E5.top"),sQuery(id+"F13.wireOp",EDGE,"E5.left")])]});
            var Q10;
            Q10=makeQuery(id+"F12.opExtrude","CAP_EDGE",EDGE,{"disambiguationData":[OSD([sQuery(id+"F11.wireOp",EDGE,"E4.top")])],"isStart":false});
            var Q11;
            Q11=makeQuery(id+"F14.opExtrude","SWEPT_EDGE",EDGE,{"disambiguationData":[OSD([sQuery(id+"F9.wireOp",EDGE,"E3.right"),sQuery(id+"F11.wireOp",EDGE,"E4.bottom"),sQuery(id+"F11.wireOp",EDGE,"E4.left"),sQuery(id+"F13.wireOp",EDGE,"E5.bottom"),sQuery(id+"F13.wireOp",EDGE,"E5.left")])]});
            var Q12;
            Q12=makeQuery(id+"F14.opExtrude","SWEPT_FACE",FACE,{"disambiguationData":[OSD([sQuery(id+"F13.wireOp",EDGE,"E5.bottom")])]});
            var Q13;
            Q13=makeQuery(id+"F10.opExtrude","SWEPT_FACE",FACE,{"disambiguationData":[OSD([sQuery(id+"F9.wireOp",EDGE,"E3.right")])]});
            var Q14;
            Q14=makeQuery(id+"F10.opExtrude","CAP_EDGE",EDGE,{"disambiguationData":[OSD([sQuery(id+"F9.wireOp",EDGE,"E3.right")])],"isStart":false});
            var Q15;
            Q15=makeQuery(id+"F14.opExtrude","SWEPT_FACE",FACE,{"disambiguationData":[OSD([sQuery(id+"F13.wireOp",EDGE,"E5.left")])]});
            var Q16;
            Q16=makeQuery(id+"F14.boolean.opBoolean","MERGE",EDGE,{"derivedFrom":[makeQuery(id+"F10.opExtrude","SWEPT_EDGE",EDGE,{"disambiguationData":[OSD([sQuery(id+"F9.wireOp",EDGE,"E3.top"),sQuery(id+"F9.wireOp",EDGE,"E3.left")])]}),makeQuery(id+"F14.opExtrude","SWEPT_EDGE",EDGE,{"disambiguationData":[OSD([sQuery(id+"F13.wireOp",EDGE,"E5.top"),sQuery(id+"F13.wireOp",EDGE,"E5.right")])]})]});
            var Q17;
            Q17=makeQuery(id+"F14.boolean.opBoolean","MERGE",FACE,{"derivedFrom":[makeQuery(id+"F12.boolean.opBoolean","MERGE",FACE,{"derivedFrom":[makeQuery(id+"F10.opExtrude","SWEPT_FACE",FACE,{"disambiguationData":[OSD([sQuery(id+"F9.wireOp",EDGE,"E3.top")])]}),makeQuery(id+"F12.opExtrude","SWEPT_FACE",FACE,{"disambiguationData":[OSD([sQuery(id+"F11.wireOp",EDGE,"E4.right")])]})]}),makeQuery(id+"F14.opExtrude","SWEPT_FACE",FACE,{"disambiguationData":[OSD([sQuery(id+"F13.wireOp",EDGE,"E5.top")])]})]});
            var Q18;
            {var subQ0=sQuery(id+"F9.wireOp",EDGE,"E3.right");var subQ1=sQuery(id+"F9.wireOp",EDGE,"E3.bottom");var subQ2=sQuery(id+"F9.wireOp",EDGE,"E3.left");var subQ3=makeQuery(id+"F12.opExtrude","SWEPT_FACE",FACE,{"disambiguationData":[OSD([sQuery(id+"F11.wireOp",EDGE,"E4.bottom")])]});var subQ4=makeQuery(id+"F10.opExtrude","CAP_FACE",FACE,{"disambiguationData":[OSD([subQ1,sQuery(id+"F9.wireOp",EDGE,"E3.top"),subQ2,subQ0])],"isStart":false});Q18=makeQuery(id+"F14.boolean.opBoolean","SPLIT",FACE,{"disambiguationData":[TD([makeQuery(id+"F10.opExtrude","SWEPT_FACE",FACE,{"disambiguationData":[OSD([subQ1])]})])],"derivedFrom":makeQuery(id+"F12.boolean.opBoolean","MERGE",FACE,{"derivedFrom":[subQ4,subQ3]})});}
            var Q19;
            Q19=makeQuery(id+"F12.boolean.opBoolean","MERGE",EDGE,{"derivedFrom":[makeQuery(id+"F10.opExtrude","CAP_EDGE",EDGE,{"disambiguationData":[OSD([sQuery(id+"F9.wireOp",EDGE,"E3.top")])],"isStart":false}),makeQuery(id+"F12.opExtrude","SWEPT_EDGE",EDGE,{"disambiguationData":[OSD([sQuery(id+"F11.wireOp",EDGE,"E4.bottom"),sQuery(id+"F11.wireOp",EDGE,"E4.right")])]})]});
            var Q20;
            Q20=makeQuery(id+"F14.opExtrude","CAP_EDGE",EDGE,{"disambiguationData":[OSD([sQuery(id+"F13.wireOp",EDGE,"E5.left")])],"isStart":false});
            var Q21;
            {var subQ0=sQuery(id+"F9.wireOp",EDGE,"E3.right");var subQ1=sQuery(id+"F9.wireOp",EDGE,"E3.top");var subQ2=sQuery(id+"F11.wireOp",EDGE,"E4.bottom");var subQ3=makeQuery(id+"F12.opExtrude","SWEPT_FACE",FACE,{"disambiguationData":[OSD([subQ2])]});var subQ4=makeQuery(id+"F10.opExtrude","CAP_FACE",FACE,{"disambiguationData":[OSD([sQuery(id+"F9.wireOp",EDGE,"E3.bottom"),subQ1,sQuery(id+"F9.wireOp",EDGE,"E3.left"),subQ0])],"isStart":false});Q21=makeQuery(id+"F14.boolean.opBoolean","SPLIT",FACE,{"disambiguationData":[TD([makeQuery(id+"F10.opExtrude","SWEPT_FACE",FACE,{"disambiguationData":[OSD([subQ1])]})])],"derivedFrom":makeQuery(id+"F12.boolean.opBoolean","MERGE",FACE,{"derivedFrom":[subQ4,subQ3]})});}
            var Q22;
            Q22=makeQuery(id+"F14.opExtrude","CAP_EDGE",EDGE,{"disambiguationData":[OSD([sQuery(id+"F13.wireOp",EDGE,"E5.left")])],"isStart":true});
            var Q23;
            Q23=makeQuery(id+"F14.opExtrude","CAP_EDGE",EDGE,{"disambiguationData":[OSD([sQuery(id+"F13.wireOp",EDGE,"E5.right")])],"isStart":false});
            var Q24;
            Q24=makeQuery(id+"F10.opExtrude","CAP_EDGE",EDGE,{"disambiguationData":[OSD([sQuery(id+"F9.wireOp",EDGE,"E3.bottom")])],"isStart":true});
            var Q25;
            Q25=makeQuery(id+"F14.opExtrude","SWEPT_EDGE",EDGE,{"disambiguationData":[OSD([sQuery(id+"F9.wireOp",EDGE,"E3.left"),sQuery(id+"F13.wireOp",EDGE,"E5.bottom"),sQuery(id+"F13.wireOp",EDGE,"E5.right")])]});
            var Q26;
            Q26=makeQuery(id+"F10.opExtrude","CAP_EDGE",EDGE,{"disambiguationData":[OSD([sQuery(id+"F9.wireOp",EDGE,"E3.bottom")])],"isStart":false});
            var Q27;
            Q27=makeQuery(id+"F12.opExtrude","SWEPT_EDGE",EDGE,{"disambiguationData":[OSD([sQuery(id+"F9.wireOp",EDGE,"E3.right"),sQuery(id+"F11.wireOp",EDGE,"E4.top"),sQuery(id+"F11.wireOp",EDGE,"E4.left")])]});
            var Q28;
            Q28=makeQuery(id+"F10.opExtrude","CAP_EDGE",EDGE,{"disambiguationData":[OSD([sQuery(id+"F9.wireOp",EDGE,"E3.left")])],"isStart":true});
            var Q29;
            Q29=makeQuery(id+"F10.opExtrude","CAP_EDGE",EDGE,{"disambiguationData":[OSD([sQuery(id+"F9.wireOp",EDGE,"E3.right")])],"isStart":true});
            var Q30;
            Q30=makeQuery(id+"F12.opExtrude","CAP_EDGE",EDGE,{"disambiguationData":[OSD([sQuery(id+"F11.wireOp",EDGE,"E4.left")])],"isStart":false});
            var Q31;
            Q31=makeQuery(id+"F12.opExtrude","CAP_EDGE",EDGE,{"disambiguationData":[OSD([sQuery(id+"F11.wireOp",EDGE,"E4.left")])],"isStart":true});
            var Q32;
            Q32=makeQuery(id+"F12.opExtrude","CAP_EDGE",EDGE,{"disambiguationData":[OSD([sQuery(id+"F11.wireOp",EDGE,"E4.right")])],"isStart":false});
            var Q33;
            Q33=makeQuery(id+"F14.opExtrude","CAP_EDGE",EDGE,{"disambiguationData":[OSD([sQuery(id+"F13.wireOp",EDGE,"E5.bottom")])],"isStart":false});
            var Q34;
            Q34=makeQuery(id+"F14.boolean.opBoolean","MERGE",FACE,{"derivedFrom":[makeQuery(id+"F10.opExtrude","SWEPT_FACE",FACE,{"disambiguationData":[OSD([sQuery(id+"F9.wireOp",EDGE,"E3.left")])]}),makeQuery(id+"F14.opExtrude","SWEPT_FACE",FACE,{"disambiguationData":[OSD([sQuery(id+"F13.wireOp",EDGE,"E5.right")])]})]});
            var Q35;
            Q35=makeQuery(id+"F14.opExtrude","CAP_EDGE",EDGE,{"disambiguationData":[OSD([sQuery(id+"F13.wireOp",EDGE,"E5.top")])],"isStart":false});
            var Q36;
            Q36=makeQuery(id+"F10.opExtrude","CAP_EDGE",EDGE,{"disambiguationData":[OSD([sQuery(id+"F9.wireOp",EDGE,"E3.left")])],"isStart":false});
            var Q37;
            Q37=makeQuery(id+"F14.opExtrude","CAP_EDGE",EDGE,{"disambiguationData":[OSD([sQuery(id+"F13.wireOp",EDGE,"E5.bottom")])],"isStart":true});
            var Q38;
            Q38=makeQuery(id+"F10.opExtrude","SWEPT_EDGE",EDGE,{"disambiguationData":[OSD([sQuery(id+"F9.wireOp",EDGE,"E3.bottom"),sQuery(id+"F9.wireOp",EDGE,"E3.left")])]});
            fillet(context, id + "F15", {"entities" : qUnion([Q0, Q1, Q2, Q3, Q4, Q5, Q6, Q7, Q8, Q9, Q10, Q11, Q12, Q13, Q14, Q15, Q16, Q17, Q18, Q19, Q20, Q21, Q22, Q23, Q24, Q25, Q26, Q27, Q28, Q29, Q30, Q31, Q32, Q33, Q34, Q35, Q36, Q37, Q38]), "radius" : 1.27 * mm, "tangentPropagation" : true, "allowEdgeOverflow" : false});
        }
        {
            var Q0;
            Q0=qCreatedBy(makeId("Top.planeOp"),FACE);
            var sketch = newSketch(context, id + "F16", { "sketchPlane" : qUnion([Q0])});
            skLineSegment(sketch, "E6.bottom", {"start": v(68.13, 68.75) * mm, "end": v(55.43, 68.75) * mm});
            skLineSegment(sketch, "E6.top", {"start": v(68.13, 56.05) * mm, "end": v(55.43, 56.05) * mm});
            skLineSegment(sketch, "E6.left", {"start": v(68.13, 68.75) * mm, "end": v(68.13, 56.05) * mm});
            skLineSegment(sketch, "E6.right", {"start": v(55.43, 68.75) * mm, "end": v(55.43, 56.05) * mm});
            skSolve(sketch);
        }
        {
            var Q0;
            Q0 = qSketchRegion(id + "F16", true);
            extrude(context, id + "F17", {"entities" : qUnion([Q0]), "depth" : 50.8 * mm});
        }
        {
            var Q0;
            Q0=makeQuery(id+"F17.opExtrude","CAP_EDGE",EDGE,{"disambiguationData":[OSD([sQuery(id+"F16.wireOp",EDGE,"E6.top")])],"isStart":false});
            var Q1;
            Q1=makeQuery(id+"F17.opExtrude","CAP_EDGE",EDGE,{"disambiguationData":[OSD([sQuery(id+"F16.wireOp",EDGE,"E6.left")])],"isStart":true});
            var Q2;
            Q2=makeQuery(id+"F17.opExtrude","SWEPT_FACE",FACE,{"disambiguationData":[OSD([sQuery(id+"F16.wireOp",EDGE,"E6.bottom")])]});
            var Q3;
            Q3=makeQuery(id+"F17.opExtrude","SWEPT_EDGE",EDGE,{"disambiguationData":[OSD([sQuery(id+"F16.wireOp",EDGE,"E6.bottom"),sQuery(id+"F16.wireOp",EDGE,"E6.left")])]});
            var Q4;
            Q4=makeQuery(id+"F17.opExtrude","CAP_FACE",FACE,{"disambiguationData":[OSD([sQuery(id+"F16.wireOp",EDGE,"E6.bottom"),sQuery(id+"F16.wireOp",EDGE,"E6.top"),sQuery(id+"F16.wireOp",EDGE,"E6.left"),sQuery(id+"F16.wireOp",EDGE,"E6.right")])],"isStart":true});
            var Q5;
            Q5=makeQuery(id+"F17.opExtrude","CAP_FACE",FACE,{"disambiguationData":[OSD([sQuery(id+"F16.wireOp",EDGE,"E6.bottom"),sQuery(id+"F16.wireOp",EDGE,"E6.top"),sQuery(id+"F16.wireOp",EDGE,"E6.left"),sQuery(id+"F16.wireOp",EDGE,"E6.right")])],"isStart":false});
            var Q6;
            Q6=makeQuery(id+"F17.opExtrude","SWEPT_EDGE",EDGE,{"disambiguationData":[OSD([sQuery(id+"F16.wireOp",EDGE,"E6.top"),sQuery(id+"F16.wireOp",EDGE,"E6.left")])]});
            var Q7;
            Q7=makeQuery(id+"F17.opExtrude","SWEPT_FACE",FACE,{"disambiguationData":[OSD([sQuery(id+"F16.wireOp",EDGE,"E6.top")])]});
            var Q8;
            Q8=makeQuery(id+"F17.opExtrude","SWEPT_EDGE",EDGE,{"disambiguationData":[OSD([sQuery(id+"F16.wireOp",EDGE,"E6.top"),sQuery(id+"F16.wireOp",EDGE,"E6.right")])]});
            var Q9;
            Q9=makeQuery(id+"F17.opExtrude","SWEPT_FACE",FACE,{"disambiguationData":[OSD([sQuery(id+"F16.wireOp",EDGE,"E6.left")])]});
            var Q10;
            Q10=makeQuery(id+"F17.opExtrude","SWEPT_FACE",FACE,{"disambiguationData":[OSD([sQuery(id+"F16.wireOp",EDGE,"E6.right")])]});
            var Q11;
            Q11=makeQuery(id+"F17.opExtrude","CAP_EDGE",EDGE,{"disambiguationData":[OSD([sQuery(id+"F16.wireOp",EDGE,"E6.left")])],"isStart":false});
            var Q12;
            Q12=makeQuery(id+"F17.opExtrude","CAP_EDGE",EDGE,{"disambiguationData":[OSD([sQuery(id+"F16.wireOp",EDGE,"E6.right")])],"isStart":true});
            var Q13;
            Q13=makeQuery(id+"F17.opExtrude","CAP_EDGE",EDGE,{"disambiguationData":[OSD([sQuery(id+"F16.wireOp",EDGE,"E6.right")])],"isStart":false});
            var Q14;
            Q14=makeQuery(id+"F17.opExtrude","SWEPT_EDGE",EDGE,{"disambiguationData":[OSD([sQuery(id+"F16.wireOp",EDGE,"E6.bottom"),sQuery(id+"F16.wireOp",EDGE,"E6.right")])]});
            var Q15;
            Q15=makeQuery(id+"F17.opExtrude","CAP_EDGE",EDGE,{"disambiguationData":[OSD([sQuery(id+"F16.wireOp",EDGE,"E6.bottom")])],"isStart":true});
            var Q16;
            Q16=makeQuery(id+"F17.opExtrude","CAP_EDGE",EDGE,{"disambiguationData":[OSD([sQuery(id+"F16.wireOp",EDGE,"E6.bottom")])],"isStart":false});
            var Q17;
            Q17=makeQuery(id+"F17.opExtrude","CAP_EDGE",EDGE,{"disambiguationData":[OSD([sQuery(id+"F16.wireOp",EDGE,"E6.top")])],"isStart":true});
            fillet(context, id + "F18", {"entities" : qUnion([Q0, Q1, Q2, Q3, Q4, Q5, Q6, Q7, Q8, Q9, Q10, Q11, Q12, Q13, Q14, Q15, Q16, Q17]), "radius" : 1.27 * mm, "tangentPropagation" : true, "allowEdgeOverflow" : false});
        }
        {
            var Q0;
            Q0=qCreatedBy(makeId("Top.planeOp"),FACE);
            var sketch = newSketch(context, id + "F19", { "sketchPlane" : qUnion([Q0])});
            skLineSegment(sketch, "E7.bottom", {"start": v(51.96, -50.85) * mm, "end": v(64.66, -50.85) * mm});
            skLineSegment(sketch, "E7.top", {"start": v(51.96, -63.55) * mm, "end": v(64.66, -63.55) * mm});
            skLineSegment(sketch, "E7.left", {"start": v(51.96, -50.85) * mm, "end": v(51.96, -63.55) * mm});
            skLineSegment(sketch, "E7.right", {"start": v(64.66, -50.85) * mm, "end": v(64.66, -63.55) * mm});
            skSolve(sketch);
        }
        {
            var Q0;
            Q0 = qSketchRegion(id + "F19", true);
            extrude(context, id + "F20", {"entities" : qUnion([Q0]), "depth" : 12.7 * mm});
        }
        {
            var Q0;
            Q0=makeQuery(id+"F20.opExtrude","CAP_EDGE",EDGE,{"disambiguationData":[OSD([sQuery(id+"F19.wireOp",EDGE,"E7.top")])],"isStart":false});
            var Q1;
            Q1=makeQuery(id+"F20.opExtrude","CAP_EDGE",EDGE,{"disambiguationData":[OSD([sQuery(id+"F19.wireOp",EDGE,"E7.left")])],"isStart":false});
            var Q2;
            Q2=makeQuery(id+"F20.opExtrude","CAP_EDGE",EDGE,{"disambiguationData":[OSD([sQuery(id+"F19.wireOp",EDGE,"E7.right")])],"isStart":true});
            var Q3;
            Q3=makeQuery(id+"F20.opExtrude","CAP_EDGE",EDGE,{"disambiguationData":[OSD([sQuery(id+"F19.wireOp",EDGE,"E7.right")])],"isStart":false});
            var Q4;
            Q4=makeQuery(id+"F20.opExtrude","SWEPT_FACE",FACE,{"disambiguationData":[OSD([sQuery(id+"F19.wireOp",EDGE,"E7.bottom")])]});
            var Q5;
            Q5=makeQuery(id+"F20.opExtrude","CAP_FACE",FACE,{"disambiguationData":[OSD([sQuery(id+"F19.wireOp",EDGE,"E7.bottom"),sQuery(id+"F19.wireOp",EDGE,"E7.top"),sQuery(id+"F19.wireOp",EDGE,"E7.left"),sQuery(id+"F19.wireOp",EDGE,"E7.right")])],"isStart":true});
            var Q6;
            Q6=makeQuery(id+"F20.opExtrude","SWEPT_EDGE",EDGE,{"disambiguationData":[OSD([sQuery(id+"F19.wireOp",EDGE,"E7.bottom"),sQuery(id+"F19.wireOp",EDGE,"E7.right")])]});
            var Q7;
            Q7=makeQuery(id+"F20.opExtrude","CAP_FACE",FACE,{"disambiguationData":[OSD([sQuery(id+"F19.wireOp",EDGE,"E7.bottom"),sQuery(id+"F19.wireOp",EDGE,"E7.top"),sQuery(id+"F19.wireOp",EDGE,"E7.left"),sQuery(id+"F19.wireOp",EDGE,"E7.right")])],"isStart":false});
            var Q8;
            Q8=makeQuery(id+"F20.opExtrude","SWEPT_EDGE",EDGE,{"disambiguationData":[OSD([sQuery(id+"F19.wireOp",EDGE,"E7.top"),sQuery(id+"F19.wireOp",EDGE,"E7.left")])]});
            var Q9;
            Q9=makeQuery(id+"F20.opExtrude","SWEPT_FACE",FACE,{"disambiguationData":[OSD([sQuery(id+"F19.wireOp",EDGE,"E7.top")])]});
            var Q10;
            Q10=makeQuery(id+"F20.opExtrude","SWEPT_EDGE",EDGE,{"disambiguationData":[OSD([sQuery(id+"F19.wireOp",EDGE,"E7.top"),sQuery(id+"F19.wireOp",EDGE,"E7.right")])]});
            var Q11;
            Q11=makeQuery(id+"F20.opExtrude","SWEPT_FACE",FACE,{"disambiguationData":[OSD([sQuery(id+"F19.wireOp",EDGE,"E7.left")])]});
            var Q12;
            Q12=makeQuery(id+"F20.opExtrude","SWEPT_FACE",FACE,{"disambiguationData":[OSD([sQuery(id+"F19.wireOp",EDGE,"E7.right")])]});
            var Q13;
            Q13=makeQuery(id+"F20.opExtrude","CAP_EDGE",EDGE,{"disambiguationData":[OSD([sQuery(id+"F19.wireOp",EDGE,"E7.bottom")])],"isStart":false});
            var Q14;
            Q14=makeQuery(id+"F20.opExtrude","CAP_EDGE",EDGE,{"disambiguationData":[OSD([sQuery(id+"F19.wireOp",EDGE,"E7.top")])],"isStart":true});
            var Q15;
            Q15=makeQuery(id+"F20.opExtrude","CAP_EDGE",EDGE,{"disambiguationData":[OSD([sQuery(id+"F19.wireOp",EDGE,"E7.left")])],"isStart":true});
            var Q16;
            Q16=makeQuery(id+"F20.opExtrude","SWEPT_EDGE",EDGE,{"disambiguationData":[OSD([sQuery(id+"F19.wireOp",EDGE,"E7.bottom"),sQuery(id+"F19.wireOp",EDGE,"E7.left")])]});
            var Q17;
            Q17=makeQuery(id+"F20.opExtrude","CAP_EDGE",EDGE,{"disambiguationData":[OSD([sQuery(id+"F19.wireOp",EDGE,"E7.bottom")])],"isStart":true});
            fillet(context, id + "F21", {"entities" : qUnion([Q0, Q1, Q2, Q3, Q4, Q5, Q6, Q7, Q8, Q9, Q10, Q11, Q12, Q13, Q14, Q15, Q16, Q17]), "radius" : 1.27 * mm, "tangentPropagation" : true, "allowEdgeOverflow" : false});
        }
        {
            var Q0;
            Q0=qCreatedBy(makeId("Top.planeOp"),FACE);
            var sketch = newSketch(context, id + "F22", { "sketchPlane" : qUnion([Q0])});
            skLineSegment(sketch, "E8.bottom", {"start": v(-71.77, 57.27) * mm, "end": v(-46.37, 57.27) * mm});
            skLineSegment(sketch, "E8.top", {"start": v(-71.77, 44.57) * mm, "end": v(-46.37, 44.57) * mm});
            skLineSegment(sketch, "E8.left", {"start": v(-71.77, 57.27) * mm, "end": v(-71.77, 44.57) * mm});
            skLineSegment(sketch, "E8.right", {"start": v(-46.37, 57.27) * mm, "end": v(-46.37, 44.57) * mm});
            skSolve(sketch);
        }
        {
            var Q0;
            Q0 = qSketchRegion(id + "F22", true);
            extrude(context, id + "F23", {"entities" : qUnion([Q0]), "depth" : 12.7 * mm});
        }
        {
            var Q0;
            Q0=makeQuery(id+"F23.opExtrude","CAP_FACE",FACE,{"disambiguationData":[OSD([sQuery(id+"F22.wireOp",EDGE,"E8.bottom"),sQuery(id+"F22.wireOp",EDGE,"E8.top"),sQuery(id+"F22.wireOp",EDGE,"E8.left"),sQuery(id+"F22.wireOp",EDGE,"E8.right")])],"isStart":false});
            var sketch = newSketch(context, id + "F24", { "sketchPlane" : qUnion([Q0])});
            skLineSegment(sketch, "E9.bottom", {"start": v(-59.07, 57.27) * mm, "end": v(-46.37, 57.27) * mm});
            skLineSegment(sketch, "E9.top", {"start": v(-59.07, 44.57) * mm, "end": v(-46.37, 44.57) * mm});
            skLineSegment(sketch, "E9.left", {"start": v(-59.07, 57.27) * mm, "end": v(-59.07, 44.57) * mm});
            skLineSegment(sketch, "E9.right", {"start": v(-46.37, 57.27) * mm, "end": v(-46.37, 44.57) * mm});
            skSolve(sketch);
        }
        {
            var Q0;
            Q0 = qSketchRegion(id + "F24", true);
            extrude(context, id + "F25", {"entities" : qUnion([Q0]), "operationType" : NewBodyOperationType.ADD, "depth" : 25.4 * mm});
        }
        {
            var Q0;
            Q0=makeQuery(id+"F25.boolean.opBoolean","MERGE",EDGE,{"derivedFrom":[makeQuery(id+"F23.opExtrude","SWEPT_EDGE",EDGE,{"disambiguationData":[OSD([sQuery(id+"F22.wireOp",EDGE,"E8.bottom"),sQuery(id+"F22.wireOp",EDGE,"E8.right")])]}),makeQuery(id+"F25.opExtrude","SWEPT_EDGE",EDGE,{"disambiguationData":[OSD([sQuery(id+"F24.wireOp",EDGE,"E9.bottom"),sQuery(id+"F24.wireOp",EDGE,"E9.right")])]})]});
            var Q1;
            Q1=makeQuery(id+"F25.boolean.opBoolean","MERGE",FACE,{"derivedFrom":[makeQuery(id+"F23.opExtrude","SWEPT_FACE",FACE,{"disambiguationData":[OSD([sQuery(id+"F22.wireOp",EDGE,"E8.bottom")])]}),makeQuery(id+"F25.opExtrude","SWEPT_FACE",FACE,{"disambiguationData":[OSD([sQuery(id+"F24.wireOp",EDGE,"E9.bottom")])]})]});
            var Q2;
            Q2=makeQuery(id+"F23.opExtrude","CAP_FACE",FACE,{"disambiguationData":[OSD([sQuery(id+"F22.wireOp",EDGE,"E8.bottom"),sQuery(id+"F22.wireOp",EDGE,"E8.top"),sQuery(id+"F22.wireOp",EDGE,"E8.left"),sQuery(id+"F22.wireOp",EDGE,"E8.right")])],"isStart":true});
            var Q3;
            Q3=makeQuery(id+"F25.opExtrude","CAP_EDGE",EDGE,{"disambiguationData":[OSD([sQuery(id+"F24.wireOp",EDGE,"E9.bottom")])],"isStart":false});
            var Q4;
            Q4=makeQuery(id+"F25.opExtrude","SWEPT_FACE",FACE,{"disambiguationData":[OSD([sQuery(id+"F24.wireOp",EDGE,"E9.left")])]});
            var Q5;
            Q5=makeQuery(id+"F23.opExtrude","SWEPT_FACE",FACE,{"disambiguationData":[OSD([sQuery(id+"F22.wireOp",EDGE,"E8.left")])]});
            var Q6;
            Q6=makeQuery(id+"F23.opExtrude","CAP_EDGE",EDGE,{"disambiguationData":[OSD([sQuery(id+"F22.wireOp",EDGE,"E8.bottom")])],"isStart":true});
            var Q7;
            Q7=makeQuery(id+"F25.opExtrude","CAP_FACE",FACE,{"disambiguationData":[OSD([sQuery(id+"F24.wireOp",EDGE,"E9.bottom"),sQuery(id+"F24.wireOp",EDGE,"E9.top"),sQuery(id+"F24.wireOp",EDGE,"E9.left"),sQuery(id+"F24.wireOp",EDGE,"E9.right")])],"isStart":false});
            var Q8;
            Q8=makeQuery(id+"F25.opExtrude","SWEPT_EDGE",EDGE,{"disambiguationData":[OSD([sQuery(id+"F22.wireOp",EDGE,"E8.bottom"),sQuery(id+"F24.wireOp",EDGE,"E9.bottom"),sQuery(id+"F24.wireOp",EDGE,"E9.left")])]});
            var Q9;
            Q9=makeQuery(id+"F25.boolean.opBoolean","MERGE",FACE,{"derivedFrom":[makeQuery(id+"F23.opExtrude","SWEPT_FACE",FACE,{"disambiguationData":[OSD([sQuery(id+"F22.wireOp",EDGE,"E8.top")])]}),makeQuery(id+"F25.opExtrude","SWEPT_FACE",FACE,{"disambiguationData":[OSD([sQuery(id+"F24.wireOp",EDGE,"E9.top")])]})]});
            var Q10;
            Q10=makeQuery(id+"F25.boolean.opBoolean","MERGE",EDGE,{"derivedFrom":[makeQuery(id+"F23.opExtrude","SWEPT_EDGE",EDGE,{"disambiguationData":[OSD([sQuery(id+"F22.wireOp",EDGE,"E8.top"),sQuery(id+"F22.wireOp",EDGE,"E8.right")])]}),makeQuery(id+"F25.opExtrude","SWEPT_EDGE",EDGE,{"disambiguationData":[OSD([sQuery(id+"F24.wireOp",EDGE,"E9.top"),sQuery(id+"F24.wireOp",EDGE,"E9.right")])]})]});
            var Q11;
            Q11=makeQuery(id+"F25.boolean.opBoolean","MERGE",FACE,{"derivedFrom":[makeQuery(id+"F23.opExtrude","SWEPT_FACE",FACE,{"disambiguationData":[OSD([sQuery(id+"F22.wireOp",EDGE,"E8.right")])]}),makeQuery(id+"F25.opExtrude","SWEPT_FACE",FACE,{"disambiguationData":[OSD([sQuery(id+"F24.wireOp",EDGE,"E9.right")])]})]});
            var Q12;
            Q12=makeQuery(id+"F23.opExtrude","CAP_EDGE",EDGE,{"disambiguationData":[OSD([sQuery(id+"F22.wireOp",EDGE,"E8.bottom")])],"isStart":false});
            var Q13;
            Q13=makeQuery(id+"F23.opExtrude","CAP_FACE",FACE,{"disambiguationData":[OSD([sQuery(id+"F22.wireOp",EDGE,"E8.bottom"),sQuery(id+"F22.wireOp",EDGE,"E8.top"),sQuery(id+"F22.wireOp",EDGE,"E8.left"),sQuery(id+"F22.wireOp",EDGE,"E8.right")])],"isStart":false});
            var Q14;
            Q14=makeQuery(id+"F23.opExtrude","CAP_EDGE",EDGE,{"disambiguationData":[OSD([sQuery(id+"F22.wireOp",EDGE,"E8.left")])],"isStart":true});
            var Q15;
            Q15=makeQuery(id+"F23.opExtrude","CAP_EDGE",EDGE,{"disambiguationData":[OSD([sQuery(id+"F22.wireOp",EDGE,"E8.left")])],"isStart":false});
            var Q16;
            Q16=makeQuery(id+"F23.opExtrude","CAP_EDGE",EDGE,{"disambiguationData":[OSD([sQuery(id+"F22.wireOp",EDGE,"E8.right")])],"isStart":true});
            var Q17;
            Q17=makeQuery(id+"F23.opExtrude","SWEPT_EDGE",EDGE,{"disambiguationData":[OSD([sQuery(id+"F22.wireOp",EDGE,"E8.bottom"),sQuery(id+"F22.wireOp",EDGE,"E8.left")])]});
            var Q18;
            Q18=makeQuery(id+"F23.opExtrude","SWEPT_EDGE",EDGE,{"disambiguationData":[OSD([sQuery(id+"F22.wireOp",EDGE,"E8.top"),sQuery(id+"F22.wireOp",EDGE,"E8.left")])]});
            var Q19;
            Q19=makeQuery(id+"F25.opExtrude","SWEPT_EDGE",EDGE,{"disambiguationData":[OSD([sQuery(id+"F22.wireOp",EDGE,"E8.top"),sQuery(id+"F24.wireOp",EDGE,"E9.top"),sQuery(id+"F24.wireOp",EDGE,"E9.left")])]});
            var Q20;
            Q20=makeQuery(id+"F23.opExtrude","CAP_EDGE",EDGE,{"disambiguationData":[OSD([sQuery(id+"F22.wireOp",EDGE,"E8.top")])],"isStart":true});
            var Q21;
            Q21=makeQuery(id+"F25.opExtrude","CAP_EDGE",EDGE,{"disambiguationData":[OSD([sQuery(id+"F24.wireOp",EDGE,"E9.top")])],"isStart":false});
            var Q22;
            Q22=makeQuery(id+"F25.opExtrude","CAP_EDGE",EDGE,{"disambiguationData":[OSD([sQuery(id+"F24.wireOp",EDGE,"E9.left")])],"isStart":false});
            var Q23;
            Q23=makeQuery(id+"F23.opExtrude","CAP_EDGE",EDGE,{"disambiguationData":[OSD([sQuery(id+"F22.wireOp",EDGE,"E8.top")])],"isStart":false});
            var Q24;
            Q24=makeQuery(id+"F25.opExtrude","CAP_EDGE",EDGE,{"disambiguationData":[OSD([sQuery(id+"F24.wireOp",EDGE,"E9.left")])],"isStart":true});
            var Q25;
            Q25=makeQuery(id+"F25.opExtrude","CAP_EDGE",EDGE,{"disambiguationData":[OSD([sQuery(id+"F24.wireOp",EDGE,"E9.right")])],"isStart":false});
            fillet(context, id + "F26", {"entities" : qUnion([Q0, Q1, Q2, Q3, Q4, Q5, Q6, Q7, Q8, Q9, Q10, Q11, Q12, Q13, Q14, Q15, Q16, Q17, Q18, Q19, Q20, Q21, Q22, Q23, Q24, Q25]), "radius" : 1.27 * mm, "tangentPropagation" : true, "allowEdgeOverflow" : false});
        }
        {
            var Q0;
            Q0=qCreatedBy(makeId("Top.planeOp"),FACE);
            var sketch = newSketch(context, id + "F27", { "sketchPlane" : qUnion([Q0])});
            skLineSegment(sketch, "E10.bottom", {"start": v(-65.2, -71) * mm, "end": v(-52.5, -71) * mm});
            skLineSegment(sketch, "E10.top", {"start": v(-65.2, -45.6) * mm, "end": v(-52.5, -45.6) * mm});
            skLineSegment(sketch, "E10.left", {"start": v(-65.2, -71) * mm, "end": v(-65.2, -45.6) * mm});
            skLineSegment(sketch, "E10.right", {"start": v(-52.5, -71) * mm, "end": v(-52.5, -45.6) * mm});
            skLineSegment(sketch, "E11.bottom", {"start": v(-52.5, -58.3) * mm, "end": v(-39.8, -58.3) * mm});
            skLineSegment(sketch, "E11.top", {"start": v(-52.5, -32.9) * mm, "end": v(-39.8, -32.9) * mm});
            skLineSegment(sketch, "E11.left", {"start": v(-52.5, -58.3) * mm, "end": v(-52.5, -32.9) * mm});
            skLineSegment(sketch, "E11.right", {"start": v(-39.8, -58.3) * mm, "end": v(-39.8, -32.9) * mm});
            skSolve(sketch);
        }
        {
            var Q0;
            Q0 = qSketchRegion(id + "F27", true);
            extrude(context, id + "F28", {"entities" : qUnion([Q0]), "depth" : 12.7 * mm});
        }
        {
            var Q0;
            Q0=makeQuery(id+"F28.opExtrude","CAP_EDGE",EDGE,{"disambiguationData":[OSD([sQuery(id+"F27.wireOp",EDGE,"E10.top")])],"isStart":false});
            var Q1;
            Q1=makeQuery(id+"F28.opExtrude","CAP_EDGE",EDGE,{"disambiguationData":[OSD([sQuery(id+"F27.wireOp",EDGE,"E11.right")])],"isStart":false});
            var Q2;
            Q2=makeQuery(id+"F28.opExtrude","CAP_EDGE",EDGE,{"disambiguationData":[OSD([sQuery(id+"F27.wireOp",EDGE,"E11.top")])],"isStart":false});
            var Q3;
            Q3=makeQuery(id+"F28.opExtrude","CAP_EDGE",EDGE,{"disambiguationData":[OSD([sQuery(id+"F27.wireOp",EDGE,"E11.top")])],"isStart":true});
            var Q4;
            Q4=makeQuery(id+"F28.opExtrude","CAP_EDGE",EDGE,{"disambiguationData":[OSD([sQuery(id+"F27.wireOp",EDGE,"E11.bottom")])],"isStart":false});
            var Q5;
            Q5=makeQuery(id+"F28.opExtrude","CAP_EDGE",EDGE,{"disambiguationData":[OSD([sQuery(id+"F27.wireOp",EDGE,"E10.left")])],"isStart":false});
            var Q6;
            Q6=makeQuery(id+"F28.opExtrude","CAP_EDGE",EDGE,{"disambiguationData":[OSD([sQuery(id+"F27.wireOp",EDGE,"E10.right")])],"isStart":true});
            var Q7;
            Q7=makeQuery(id+"F28.opExtrude","CAP_EDGE",EDGE,{"disambiguationData":[OSD([sQuery(id+"F27.wireOp",EDGE,"E10.right")])],"isStart":false});
            var Q8;
            Q8=makeQuery(id+"F28.opExtrude","SWEPT_FACE",FACE,{"disambiguationData":[OSD([sQuery(id+"F27.wireOp",EDGE,"E10.bottom")])]});
            var Q9;
            Q9=makeQuery(id+"F28.opExtrude","CAP_EDGE",EDGE,{"disambiguationData":[OSD([sQuery(id+"F27.wireOp",EDGE,"E11.right")])],"isStart":true});
            var Q10;
            Q10=makeQuery(id+"F28.opExtrude","CAP_FACE",FACE,{"disambiguationData":[OSD([sQuery(id+"F27.wireOp",EDGE,"E10.bottom"),sQuery(id+"F27.wireOp",EDGE,"E10.top"),sQuery(id+"F27.wireOp",EDGE,"E10.left"),sQuery(id+"F27.wireOp",EDGE,"E10.right"),sQuery(id+"F27.wireOp",EDGE,"E11.bottom"),sQuery(id+"F27.wireOp",EDGE,"E11.top"),sQuery(id+"F27.wireOp",EDGE,"E11.left"),sQuery(id+"F27.wireOp",EDGE,"E11.right")])],"isStart":true});
            var Q11;
            Q11=makeQuery(id+"F28.opExtrude","SWEPT_EDGE",EDGE,{"disambiguationData":[OSD([sQuery(id+"F27.wireOp",EDGE,"E10.bottom"),sQuery(id+"F27.wireOp",EDGE,"E10.right")])]});
            var Q12;
            Q12=makeQuery(id+"F28.opExtrude","CAP_EDGE",EDGE,{"disambiguationData":[OSD([sQuery(id+"F27.wireOp",EDGE,"E11.left")])],"isStart":false});
            var Q13;
            Q13=makeQuery(id+"F28.opExtrude","CAP_FACE",FACE,{"disambiguationData":[OSD([sQuery(id+"F27.wireOp",EDGE,"E10.bottom"),sQuery(id+"F27.wireOp",EDGE,"E10.top"),sQuery(id+"F27.wireOp",EDGE,"E10.left"),sQuery(id+"F27.wireOp",EDGE,"E10.right"),sQuery(id+"F27.wireOp",EDGE,"E11.bottom"),sQuery(id+"F27.wireOp",EDGE,"E11.top"),sQuery(id+"F27.wireOp",EDGE,"E11.left"),sQuery(id+"F27.wireOp",EDGE,"E11.right")])],"isStart":false});
            var Q14;
            Q14=makeQuery(id+"F28.opExtrude","SWEPT_EDGE",EDGE,{"disambiguationData":[OSD([sQuery(id+"F27.wireOp",EDGE,"E10.top"),sQuery(id+"F27.wireOp",EDGE,"E10.left")])]});
            var Q15;
            Q15=makeQuery(id+"F28.opExtrude","SWEPT_FACE",FACE,{"disambiguationData":[OSD([sQuery(id+"F27.wireOp",EDGE,"E10.top")])]});
            var Q16;
            Q16=makeQuery(id+"F28.opExtrude","SWEPT_FACE",FACE,{"disambiguationData":[OSD([sQuery(id+"F27.wireOp",EDGE,"E10.left")])]});
            var Q17;
            Q17=makeQuery(id+"F28.opExtrude","SWEPT_FACE",FACE,{"disambiguationData":[OSD([sQuery(id+"F27.wireOp",EDGE,"E10.right")])]});
            var Q18;
            Q18=makeQuery(id+"F28.opExtrude","SWEPT_EDGE",EDGE,{"disambiguationData":[OSD([sQuery(id+"F27.wireOp",EDGE,"E11.bottom"),sQuery(id+"F27.wireOp",EDGE,"E11.right")])]});
            var Q19;
            Q19=makeQuery(id+"F28.opExtrude","SWEPT_EDGE",EDGE,{"disambiguationData":[OSD([sQuery(id+"F27.wireOp",EDGE,"E11.top"),sQuery(id+"F27.wireOp",EDGE,"E11.left")])]});
            var Q20;
            Q20=makeQuery(id+"F28.opExtrude","SWEPT_FACE",FACE,{"disambiguationData":[OSD([sQuery(id+"F27.wireOp",EDGE,"E11.bottom")])]});
            var Q21;
            Q21=makeQuery(id+"F28.opExtrude","SWEPT_FACE",FACE,{"disambiguationData":[OSD([sQuery(id+"F27.wireOp",EDGE,"E11.top")])]});
            var Q22;
            Q22=makeQuery(id+"F28.opExtrude","SWEPT_EDGE",EDGE,{"disambiguationData":[OSD([sQuery(id+"F27.wireOp",EDGE,"E11.top"),sQuery(id+"F27.wireOp",EDGE,"E11.right")])]});
            var Q23;
            Q23=makeQuery(id+"F28.opExtrude","SWEPT_FACE",FACE,{"disambiguationData":[OSD([sQuery(id+"F27.wireOp",EDGE,"E11.left")])]});
            var Q24;
            Q24=makeQuery(id+"F28.opExtrude","SWEPT_FACE",FACE,{"disambiguationData":[OSD([sQuery(id+"F27.wireOp",EDGE,"E11.right")])]});
            var Q25;
            Q25=makeQuery(id+"F28.opExtrude","CAP_EDGE",EDGE,{"disambiguationData":[OSD([sQuery(id+"F27.wireOp",EDGE,"E10.bottom")])],"isStart":false});
            var Q26;
            Q26=makeQuery(id+"F28.opExtrude","CAP_EDGE",EDGE,{"disambiguationData":[OSD([sQuery(id+"F27.wireOp",EDGE,"E10.top")])],"isStart":true});
            var Q27;
            Q27=makeQuery(id+"F28.opExtrude","CAP_EDGE",EDGE,{"disambiguationData":[OSD([sQuery(id+"F27.wireOp",EDGE,"E10.left")])],"isStart":true});
            var Q28;
            Q28=makeQuery(id+"F28.opExtrude","CAP_EDGE",EDGE,{"disambiguationData":[OSD([sQuery(id+"F27.wireOp",EDGE,"E11.bottom")])],"isStart":true});
            var Q29;
            Q29=makeQuery(id+"F28.opExtrude","SWEPT_EDGE",EDGE,{"disambiguationData":[OSD([sQuery(id+"F27.wireOp",EDGE,"E10.bottom"),sQuery(id+"F27.wireOp",EDGE,"E10.left")])]});
            var Q30;
            Q30=makeQuery(id+"F28.opExtrude","CAP_EDGE",EDGE,{"disambiguationData":[OSD([sQuery(id+"F27.wireOp",EDGE,"E11.left")])],"isStart":true});
            var Q31;
            Q31=makeQuery(id+"F28.opExtrude","SWEPT_EDGE",EDGE,{"disambiguationData":[OSD([sQuery(id+"F27.wireOp",EDGE,"E10.top"),sQuery(id+"F27.wireOp",EDGE,"E11.left")])]});
            var Q32;
            Q32=makeQuery(id+"F28.opExtrude","SWEPT_EDGE",EDGE,{"disambiguationData":[OSD([sQuery(id+"F27.wireOp",EDGE,"E10.right"),sQuery(id+"F27.wireOp",EDGE,"E11.bottom"),sQuery(id+"F27.wireOp",EDGE,"E11.left")])]});
            var Q33;
            Q33=makeQuery(id+"F28.opExtrude","CAP_EDGE",EDGE,{"disambiguationData":[OSD([sQuery(id+"F27.wireOp",EDGE,"E10.bottom")])],"isStart":true});
            fillet(context, id + "F29", {"entities" : qUnion([Q0, Q1, Q2, Q3, Q4, Q5, Q6, Q7, Q8, Q9, Q10, Q11, Q12, Q13, Q14, Q15, Q16, Q17, Q18, Q19, Q20, Q21, Q22, Q23, Q24, Q25, Q26, Q27, Q28, Q29, Q30, Q31, Q32, Q33]), "radius" : 1.27 * mm, "tangentPropagation" : true, "allowEdgeOverflow" : false});
        }
        {
            var Q0;
            Q0=qCreatedBy(makeId("Top.planeOp"),FACE);
            var sketch = newSketch(context, id + "F30", { "sketchPlane" : qUnion([Q0])});
            skLineSegment(sketch, "E12.rect.bottom", {"start": v(2.07, 56.5) * mm, "end": v(-10.63, 56.5) * mm});
            skLineSegment(sketch, "E12.rect.top", {"start": v(2.07, 43.8) * mm, "end": v(-10.63, 43.8) * mm});
            skLineSegment(sketch, "E12.rect.left", {"start": v(2.07, 56.5) * mm, "end": v(2.07, 43.8) * mm});
            skLineSegment(sketch, "E12.rect.right", {"start": v(-10.63, 56.5) * mm, "end": v(-10.63, 43.8) * mm});
            skPoint(sketch, "E12.rect.middle", {"position": v(-4.28, 50.16) * mm});
            skSolve(sketch);
        }
        {
            var Q0;
            Q0 = qSketchRegion(id + "F30", true);
            extrude(context, id + "F31", {"entities" : qUnion([Q0]), "depth" : 12.7 * mm});
        }
        {
            var Q0;
            Q0=makeQuery(id+"F31.opExtrude","CAP_FACE",FACE,{"disambiguationData":[OSD([sQuery(id+"F30.wireOp",EDGE,"E12.rect.bottom"),sQuery(id+"F30.wireOp",EDGE,"E12.rect.top"),sQuery(id+"F30.wireOp",EDGE,"E12.rect.left"),sQuery(id+"F30.wireOp",EDGE,"E12.rect.right")])],"isStart":false});
            var sketch = newSketch(context, id + "F32", { "sketchPlane" : qUnion([Q0])});
            skPoint(sketch, "E13", {"position": v(-10.63, 50.16) * mm});
            skPoint(sketch, "E14", {"position": v(-4.28, 56.5) * mm});
            skPoint(sketch, "E15", {"position": v(-4.28, 50.16) * mm});
            skLineSegment(sketch, "E16.rect.bottom", {"start": v(14.77, 56.5) * mm, "end": v(-23.33, 56.5) * mm});
            skLineSegment(sketch, "E16.rect.top", {"start": v(14.77, 43.8) * mm, "end": v(-23.33, 43.8) * mm});
            skLineSegment(sketch, "E16.rect.left", {"start": v(14.77, 56.5) * mm, "end": v(14.77, 43.8) * mm});
            skLineSegment(sketch, "E16.rect.right", {"start": v(-23.33, 56.5) * mm, "end": v(-23.33, 43.8) * mm});
            skSolve(sketch);
        }
        {
            var Q0;
            Q0 = qSketchRegion(id + "F32", true);
            extrude(context, id + "F33", {"entities" : qUnion([Q0]), "operationType" : NewBodyOperationType.ADD, "depth" : 12.7 * mm});
        }
        {
            var Q0;
            Q0=makeQuery(id+"F33.opExtrude","CAP_FACE",FACE,{"disambiguationData":[OSD([sQuery(id+"F32.wireOp",EDGE,"E16.rect.bottom"),sQuery(id+"F32.wireOp",EDGE,"E16.rect.top"),sQuery(id+"F32.wireOp",EDGE,"E16.rect.left"),sQuery(id+"F32.wireOp",EDGE,"E16.rect.right")])],"isStart":false});
            var Q1;
            Q1=makeQuery(id+"F33.boolean.opBoolean","MERGE",FACE,{"derivedFrom":[makeQuery(id+"F31.opExtrude","SWEPT_FACE",FACE,{"disambiguationData":[OSD([sQuery(id+"F30.wireOp",EDGE,"E12.rect.bottom")])]}),makeQuery(id+"F33.opExtrude","SWEPT_FACE",FACE,{"disambiguationData":[OSD([sQuery(id+"F32.wireOp",EDGE,"E16.rect.bottom")])]})]});
            var Q2;
            Q2=makeQuery(id+"F33.boolean.opBoolean","MERGE",FACE,{"derivedFrom":[makeQuery(id+"F31.opExtrude","SWEPT_FACE",FACE,{"disambiguationData":[OSD([sQuery(id+"F30.wireOp",EDGE,"E12.rect.top")])]}),makeQuery(id+"F33.opExtrude","SWEPT_FACE",FACE,{"disambiguationData":[OSD([sQuery(id+"F32.wireOp",EDGE,"E16.rect.top")])]})]});
            var Q3;
            Q3=makeQuery(id+"F31.opExtrude","SWEPT_FACE",FACE,{"disambiguationData":[OSD([sQuery(id+"F30.wireOp",EDGE,"E12.rect.left")])]});
            var Q4;
            Q4=makeQuery(id+"F31.opExtrude","SWEPT_FACE",FACE,{"disambiguationData":[OSD([sQuery(id+"F30.wireOp",EDGE,"E12.rect.right")])]});
            var Q5;
            Q5=makeQuery(id+"F31.opExtrude","CAP_FACE",FACE,{"disambiguationData":[OSD([sQuery(id+"F30.wireOp",EDGE,"E12.rect.bottom"),sQuery(id+"F30.wireOp",EDGE,"E12.rect.top"),sQuery(id+"F30.wireOp",EDGE,"E12.rect.left"),sQuery(id+"F30.wireOp",EDGE,"E12.rect.right")])],"isStart":true});
            var Q6;
            Q6=makeQuery(id+"F33.opExtrude","SWEPT_FACE",FACE,{"disambiguationData":[OSD([sQuery(id+"F32.wireOp",EDGE,"E16.rect.left")])]});
            var Q7;
            Q7=makeQuery(id+"F33.opExtrude","SWEPT_FACE",FACE,{"disambiguationData":[OSD([sQuery(id+"F32.wireOp",EDGE,"E16.rect.right")])]});
            var Q8;
            Q8=makeQuery(id+"F33.opExtrude","CAP_EDGE",EDGE,{"disambiguationData":[OSD([sQuery(id+"F32.wireOp",EDGE,"E16.rect.bottom")])],"isStart":false});
            var Q9;
            Q9=makeQuery(id+"F33.opExtrude","CAP_EDGE",EDGE,{"disambiguationData":[OSD([sQuery(id+"F32.wireOp",EDGE,"E16.rect.top")])],"isStart":false});
            var Q10;
            {var subQ0=sQuery(id+"F32.wireOp",EDGE,"E16.rect.top");var subQ1=sQuery(id+"F32.wireOp",EDGE,"E16.rect.bottom");var subQ2=sQuery(id+"F32.wireOp",EDGE,"E16.rect.left");Q10=makeQuery(id+"F33.boolean.opBoolean","SPLIT",FACE,{"disambiguationData":[TD([makeQuery(id+"F31.opExtrude","SWEPT_FACE",FACE,{"disambiguationData":[OSD([sQuery(id+"F30.wireOp",EDGE,"E12.rect.left")])]})])],"derivedFrom":makeQuery(id+"F33.opExtrude","CAP_FACE",FACE,{"disambiguationData":[OSD([subQ1,subQ0,subQ2,sQuery(id+"F32.wireOp",EDGE,"E16.rect.right")])],"isStart":true})});}
            var Q11;
            {var subQ0=sQuery(id+"F32.wireOp",EDGE,"E16.rect.right");var subQ1=sQuery(id+"F32.wireOp",EDGE,"E16.rect.bottom");var subQ2=sQuery(id+"F32.wireOp",EDGE,"E16.rect.top");Q11=makeQuery(id+"F33.boolean.opBoolean","SPLIT",FACE,{"disambiguationData":[TD([makeQuery(id+"F31.opExtrude","SWEPT_FACE",FACE,{"disambiguationData":[OSD([sQuery(id+"F30.wireOp",EDGE,"E12.rect.right")])]})])],"derivedFrom":makeQuery(id+"F33.opExtrude","CAP_FACE",FACE,{"disambiguationData":[OSD([subQ1,subQ2,sQuery(id+"F32.wireOp",EDGE,"E16.rect.left"),subQ0])],"isStart":true})});}
            var Q12;
            Q12=makeQuery(id+"F33.opExtrude","CAP_EDGE",EDGE,{"disambiguationData":[OSD([sQuery(id+"F32.wireOp",EDGE,"E16.rect.right")])],"isStart":false});
            var Q13;
            Q13=makeQuery(id+"F31.opExtrude","CAP_EDGE",EDGE,{"disambiguationData":[OSD([sQuery(id+"F30.wireOp",EDGE,"E12.rect.bottom")])],"isStart":true});
            var Q14;
            Q14=makeQuery(id+"F31.opExtrude","CAP_EDGE",EDGE,{"disambiguationData":[OSD([sQuery(id+"F30.wireOp",EDGE,"E12.rect.top")])],"isStart":true});
            var Q15;
            Q15=makeQuery(id+"F31.opExtrude","CAP_EDGE",EDGE,{"disambiguationData":[OSD([sQuery(id+"F30.wireOp",EDGE,"E12.rect.left")])],"isStart":false});
            var Q16;
            Q16=makeQuery(id+"F31.opExtrude","CAP_EDGE",EDGE,{"disambiguationData":[OSD([sQuery(id+"F30.wireOp",EDGE,"E12.rect.right")])],"isStart":false});
            var Q17;
            {var subQ1=sQuery(id+"F32.wireOp",EDGE,"E16.rect.bottom");Q17=makeQuery(id+"F33.boolean.opBoolean","SPLIT",EDGE,{"disambiguationData":[TD([makeQuery(id+"F31.opExtrude","SWEPT_FACE",FACE,{"disambiguationData":[OSD([sQuery(id+"F30.wireOp",EDGE,"E12.rect.left")])]})])],"derivedFrom":makeQuery(id+"F33.opExtrude","CAP_EDGE",EDGE,{"disambiguationData":[OSD([subQ1])],"isStart":true})});}
            var Q18;
            {var subQ1=sQuery(id+"F32.wireOp",EDGE,"E16.rect.bottom");Q18=makeQuery(id+"F33.boolean.opBoolean","SPLIT",EDGE,{"disambiguationData":[TD([makeQuery(id+"F31.opExtrude","SWEPT_FACE",FACE,{"disambiguationData":[OSD([sQuery(id+"F30.wireOp",EDGE,"E12.rect.right")])]})])],"derivedFrom":makeQuery(id+"F33.opExtrude","CAP_EDGE",EDGE,{"disambiguationData":[OSD([subQ1])],"isStart":true})});}
            var Q19;
            Q19=makeQuery(id+"F33.opExtrude","CAP_EDGE",EDGE,{"disambiguationData":[OSD([sQuery(id+"F32.wireOp",EDGE,"E16.rect.left")])],"isStart":false});
            var Q20;
            {var subQ0=sQuery(id+"F32.wireOp",EDGE,"E16.rect.top");Q20=makeQuery(id+"F33.boolean.opBoolean","SPLIT",EDGE,{"disambiguationData":[TD([makeQuery(id+"F31.opExtrude","SWEPT_FACE",FACE,{"disambiguationData":[OSD([sQuery(id+"F30.wireOp",EDGE,"E12.rect.left")])]})])],"derivedFrom":makeQuery(id+"F33.opExtrude","CAP_EDGE",EDGE,{"disambiguationData":[OSD([subQ0])],"isStart":true})});}
            var Q21;
            Q21=makeQuery(id+"F33.opExtrude","CAP_EDGE",EDGE,{"disambiguationData":[OSD([sQuery(id+"F32.wireOp",EDGE,"E16.rect.right")])],"isStart":true});
            var Q22;
            {var subQ1=sQuery(id+"F32.wireOp",EDGE,"E16.rect.top");Q22=makeQuery(id+"F33.boolean.opBoolean","SPLIT",EDGE,{"disambiguationData":[TD([makeQuery(id+"F31.opExtrude","SWEPT_FACE",FACE,{"disambiguationData":[OSD([sQuery(id+"F30.wireOp",EDGE,"E12.rect.right")])]})])],"derivedFrom":makeQuery(id+"F33.opExtrude","CAP_EDGE",EDGE,{"disambiguationData":[OSD([subQ1])],"isStart":true})});}
            var Q23;
            Q23=makeQuery(id+"F31.opExtrude","CAP_EDGE",EDGE,{"disambiguationData":[OSD([sQuery(id+"F30.wireOp",EDGE,"E12.rect.left")])],"isStart":true});
            var Q24;
            Q24=makeQuery(id+"F31.opExtrude","CAP_EDGE",EDGE,{"disambiguationData":[OSD([sQuery(id+"F30.wireOp",EDGE,"E12.rect.right")])],"isStart":true});
            var Q25;
            Q25=makeQuery(id+"F33.opExtrude","CAP_EDGE",EDGE,{"disambiguationData":[OSD([sQuery(id+"F32.wireOp",EDGE,"E16.rect.left")])],"isStart":true});
            fillet(context, id + "F34", {"entities" : qUnion([Q0, Q1, Q2, Q3, Q4, Q5, Q6, Q7, Q8, Q9, Q10, Q11, Q12, Q13, Q14, Q15, Q16, Q17, Q18, Q19, Q20, Q21, Q22, Q23, Q24, Q25]), "radius" : 1.27 * mm, "tangentPropagation" : true, "allowEdgeOverflow" : false});
        }
        {
            var Q0;
            Q0=qCreatedBy(makeId("Top.planeOp"),FACE);
            var sketch = newSketch(context, id + "F35", { "sketchPlane" : qUnion([Q0])});
            skLineSegment(sketch, "E17.rect.bottom", {"start": v(-61.55, 19.05) * mm, "end": v(-74.25, 19.05) * mm});
            skLineSegment(sketch, "E17.rect.top", {"start": v(-61.55, -19.05) * mm, "end": v(-74.25, -19.05) * mm});
            skLineSegment(sketch, "E17.rect.left", {"start": v(-61.55, 19.05) * mm, "end": v(-61.55, -19.05) * mm});
            skLineSegment(sketch, "E17.rect.right", {"start": v(-74.25, 19.05) * mm, "end": v(-74.25, -19.05) * mm});
            skPoint(sketch, "E17.rect.middle", {"position": v(-67.9, 0) * mm});
            skLineSegment(sketch, "E18.bottom", {"start": v(-74.25, 6.35) * mm, "end": v(-48.85, 6.35) * mm});
            skLineSegment(sketch, "E18.top", {"start": v(-74.25, -6.35) * mm, "end": v(-48.85, -6.35) * mm});
            skLineSegment(sketch, "E18.left", {"start": v(-74.25, 6.35) * mm, "end": v(-74.25, -6.35) * mm});
            skLineSegment(sketch, "E18.right", {"start": v(-48.85, 6.35) * mm, "end": v(-48.85, -6.35) * mm});
            skSolve(sketch);
        }
        {
            var Q0;
            Q0 = qSketchRegion(id + "F35", true);
            extrude(context, id + "F36", {"entities" : qUnion([Q0]), "depth" : 12.7 * mm});
        }
        {
            var Q0;
            Q0=makeQuery(id+"F36.opExtrude","CAP_FACE",FACE,{"disambiguationData":[OSD([sQuery(id+"F35.wireOp",EDGE,"E17.rect.bottom"),sQuery(id+"F35.wireOp",EDGE,"E17.rect.top"),sQuery(id+"F35.wireOp",EDGE,"E17.rect.left"),sQuery(id+"F35.wireOp",EDGE,"E17.rect.right"),sQuery(id+"F35.wireOp",EDGE,"E18.bottom"),sQuery(id+"F35.wireOp",EDGE,"E18.top"),sQuery(id+"F35.wireOp",EDGE,"E18.left"),sQuery(id+"F35.wireOp",EDGE,"E18.right")])],"isStart":false});
            var sketch = newSketch(context, id + "F37", { "sketchPlane" : qUnion([Q0])});
            skLineSegment(sketch, "E19.bottom", {"start": v(-61.55, 6.35) * mm, "end": v(-74.25, 6.35) * mm});
            skLineSegment(sketch, "E19.top", {"start": v(-61.55, -6.35) * mm, "end": v(-74.25, -6.35) * mm});
            skLineSegment(sketch, "E19.left", {"start": v(-61.55, 6.35) * mm, "end": v(-61.55, -6.35) * mm});
            skLineSegment(sketch, "E19.right", {"start": v(-74.25, 6.35) * mm, "end": v(-74.25, -6.35) * mm});
            skSolve(sketch);
        }
        {
            var Q0;
            Q0 = qSketchRegion(id + "F37", true);
            extrude(context, id + "F38", {"entities" : qUnion([Q0]), "operationType" : NewBodyOperationType.ADD, "depth" : 12.7 * mm});
        }
        {
            var Q0;
            Q0=makeQuery(id+"F38.opExtrude","SWEPT_FACE",FACE,{"disambiguationData":[OSD([sQuery(id+"F37.wireOp",EDGE,"E19.bottom")])]});
            var Q1;
            Q1=makeQuery(id+"F36.opExtrude","SWEPT_FACE",FACE,{"disambiguationData":[OSD([sQuery(id+"F35.wireOp",EDGE,"E17.rect.bottom")])]});
            var Q2;
            Q2=makeQuery(id+"F36.opExtrude","SWEPT_FACE",FACE,{"disambiguationData":[OSD([sQuery(id+"F35.wireOp",EDGE,"E17.rect.top")])]});
            var Q3;
            {var subQ0=sQuery(id+"F35.wireOp",EDGE,"E17.rect.left");Q3=makeQuery(id+"F36.opExtrude","SWEPT_FACE",FACE,{"disambiguationData":[OSD([subQ0]),TDD([makeQuery(id+"F35.imprint","IMPRINT",EDGE,{"disambiguationData":[TD([[makeQuery(id+"F35.imprint","INTERSECT",VERTEX,{"derivedFrom":[sQuery(id+"F35.wireOp",EDGE,"E17.rect.bottom"),subQ0]}),-1.0]])],"derivedFrom":subQ0})])]});}
            var Q4;
            {var subQ0=sQuery(id+"F35.wireOp",EDGE,"E17.rect.left");Q4=makeQuery(id+"F36.opExtrude","SWEPT_FACE",FACE,{"disambiguationData":[OSD([subQ0]),TDD([makeQuery(id+"F35.imprint","IMPRINT",EDGE,{"disambiguationData":[TD([[makeQuery(id+"F35.imprint","INTERSECT",VERTEX,{"derivedFrom":[sQuery(id+"F35.wireOp",EDGE,"E17.rect.top"),subQ0]}),1.0]])],"derivedFrom":subQ0})])]});}
            var Q5;
            Q5=makeQuery(id+"F36.opExtrude","SWEPT_FACE",FACE,{"disambiguationData":[OSD([sQuery(id+"F35.wireOp",EDGE,"E18.bottom")])]});
            var Q6;
            Q6=makeQuery(id+"F36.opExtrude","SWEPT_FACE",FACE,{"disambiguationData":[OSD([sQuery(id+"F35.wireOp",EDGE,"E18.top")])]});
            var Q7;
            Q7=makeQuery(id+"F36.opExtrude","SWEPT_FACE",FACE,{"disambiguationData":[OSD([sQuery(id+"F35.wireOp",EDGE,"E18.right")])]});
            var Q8;
            Q8=makeQuery(id+"F38.opExtrude","SWEPT_FACE",FACE,{"disambiguationData":[OSD([sQuery(id+"F37.wireOp",EDGE,"E19.top")])]});
            var Q9;
            Q9=makeQuery(id+"F38.opExtrude","CAP_FACE",FACE,{"disambiguationData":[OSD([sQuery(id+"F37.wireOp",EDGE,"E19.bottom"),sQuery(id+"F37.wireOp",EDGE,"E19.top"),sQuery(id+"F37.wireOp",EDGE,"E19.left"),sQuery(id+"F37.wireOp",EDGE,"E19.right")])],"isStart":false});
            var Q10;
            {var subQ0=sQuery(id+"F35.wireOp",EDGE,"E18.bottom");var subQ1=sQuery(id+"F35.wireOp",EDGE,"E18.right");var subQ2=sQuery(id+"F35.wireOp",EDGE,"E17.rect.left");var subQ3=sQuery(id+"F35.wireOp",EDGE,"E17.rect.top");var subQ4=sQuery(id+"F35.wireOp",EDGE,"E18.top");var subQ5=sQuery(id+"F35.wireOp",EDGE,"E17.rect.bottom");var subQ6=makeQuery(id+"F36.opExtrude","CAP_FACE",FACE,{"disambiguationData":[OSD([subQ5,subQ3,subQ2,sQuery(id+"F35.wireOp",EDGE,"E17.rect.right"),subQ0,subQ4,sQuery(id+"F35.wireOp",EDGE,"E18.left"),subQ1])],"isStart":false});Q10=makeQuery(id+"F38.boolean.opBoolean","SPLIT",FACE,{"disambiguationData":[TD([makeQuery(id+"F36.opExtrude","SWEPT_FACE",FACE,{"disambiguationData":[OSD([subQ1])]})])],"derivedFrom":subQ6});}
            var Q11;
            {var subQ0=sQuery(id+"F35.wireOp",EDGE,"E18.left");var subQ1=sQuery(id+"F35.wireOp",EDGE,"E17.rect.right");var subQ2=sQuery(id+"F35.wireOp",EDGE,"E17.rect.bottom");Q11=makeQuery(id+"F38.boolean.opBoolean","SPLIT",EDGE,{"disambiguationData":[TD([makeQuery(id+"F36.opExtrude","SWEPT_FACE",FACE,{"disambiguationData":[OSD([subQ2])]})])],"derivedFrom":makeQuery(id+"F36.opExtrude","CAP_EDGE",EDGE,{"disambiguationData":[OSD([subQ1,subQ0])],"isStart":false})});}
            var Q12;
            {var subQ0=sQuery(id+"F35.wireOp",EDGE,"E18.left");var subQ1=sQuery(id+"F35.wireOp",EDGE,"E17.rect.right");var subQ2=sQuery(id+"F35.wireOp",EDGE,"E18.top");var subQ3=sQuery(id+"F35.wireOp",EDGE,"E17.rect.left");var subQ4=sQuery(id+"F35.wireOp",EDGE,"E17.rect.top");var subQ5=makeQuery(id+"F36.opExtrude","CAP_FACE",FACE,{"disambiguationData":[OSD([sQuery(id+"F35.wireOp",EDGE,"E17.rect.bottom"),subQ4,subQ3,subQ1,sQuery(id+"F35.wireOp",EDGE,"E18.bottom"),subQ2,subQ0,sQuery(id+"F35.wireOp",EDGE,"E18.right")])],"isStart":false});Q12=makeQuery(id+"F38.boolean.opBoolean","SPLIT",FACE,{"disambiguationData":[TD([makeQuery(id+"F36.opExtrude","SWEPT_FACE",FACE,{"disambiguationData":[OSD([subQ4])]})])],"derivedFrom":subQ5});}
            var Q13;
            {var subQ0=sQuery(id+"F35.wireOp",EDGE,"E18.left");var subQ1=sQuery(id+"F35.wireOp",EDGE,"E17.rect.right");var subQ2=sQuery(id+"F35.wireOp",EDGE,"E17.rect.left");var subQ3=sQuery(id+"F35.wireOp",EDGE,"E17.rect.bottom");var subQ4=sQuery(id+"F35.wireOp",EDGE,"E18.bottom");var subQ5=makeQuery(id+"F36.opExtrude","CAP_FACE",FACE,{"disambiguationData":[OSD([subQ3,sQuery(id+"F35.wireOp",EDGE,"E17.rect.top"),subQ2,subQ1,subQ4,sQuery(id+"F35.wireOp",EDGE,"E18.top"),subQ0,sQuery(id+"F35.wireOp",EDGE,"E18.right")])],"isStart":false});Q13=makeQuery(id+"F38.boolean.opBoolean","SPLIT",FACE,{"disambiguationData":[TD([makeQuery(id+"F36.opExtrude","SWEPT_FACE",FACE,{"disambiguationData":[OSD([subQ3])]})])],"derivedFrom":subQ5});}
            var Q14;
            Q14=makeQuery(id+"F36.opExtrude","CAP_EDGE",EDGE,{"disambiguationData":[OSD([sQuery(id+"F35.wireOp",EDGE,"E18.right")])],"isStart":false});
            var Q15;
            {var subQ0=sQuery(id+"F35.wireOp",EDGE,"E17.rect.left");Q15=makeQuery(id+"F36.opExtrude","CAP_EDGE",EDGE,{"disambiguationData":[OSD([subQ0]),TDD([makeQuery(id+"F35.imprint","IMPRINT",EDGE,{"disambiguationData":[TD([[makeQuery(id+"F35.imprint","INTERSECT",VERTEX,{"derivedFrom":[sQuery(id+"F35.wireOp",EDGE,"E17.rect.bottom"),subQ0]}),-1.0]])],"derivedFrom":subQ0})])],"isStart":false});}
            var Q16;
            {var subQ0=sQuery(id+"F35.wireOp",EDGE,"E17.rect.left");Q16=makeQuery(id+"F36.opExtrude","CAP_EDGE",EDGE,{"disambiguationData":[OSD([subQ0]),TDD([makeQuery(id+"F35.imprint","IMPRINT",EDGE,{"disambiguationData":[TD([[makeQuery(id+"F35.imprint","INTERSECT",VERTEX,{"derivedFrom":[sQuery(id+"F35.wireOp",EDGE,"E17.rect.top"),subQ0]}),1.0]])],"derivedFrom":subQ0})])],"isStart":false});}
            var Q17;
            Q17=makeQuery(id+"F36.opExtrude","CAP_FACE",FACE,{"disambiguationData":[OSD([sQuery(id+"F35.wireOp",EDGE,"E17.rect.bottom"),sQuery(id+"F35.wireOp",EDGE,"E17.rect.top"),sQuery(id+"F35.wireOp",EDGE,"E17.rect.left"),sQuery(id+"F35.wireOp",EDGE,"E17.rect.right"),sQuery(id+"F35.wireOp",EDGE,"E18.bottom"),sQuery(id+"F35.wireOp",EDGE,"E18.top"),sQuery(id+"F35.wireOp",EDGE,"E18.left"),sQuery(id+"F35.wireOp",EDGE,"E18.right")])],"isStart":true});
            var Q18;
            Q18=makeQuery(id+"F36.opExtrude","CAP_EDGE",EDGE,{"disambiguationData":[OSD([sQuery(id+"F35.wireOp",EDGE,"E18.top")])],"isStart":false});
            var Q19;
            Q19=makeQuery(id+"F36.opExtrude","CAP_EDGE",EDGE,{"disambiguationData":[OSD([sQuery(id+"F35.wireOp",EDGE,"E18.bottom")])],"isStart":false});
            var Q20;
            Q20=makeQuery(id+"F36.opExtrude","CAP_EDGE",EDGE,{"disambiguationData":[OSD([sQuery(id+"F35.wireOp",EDGE,"E17.rect.bottom")])],"isStart":false});
            var Q21;
            Q21=makeQuery(id+"F36.opExtrude","CAP_EDGE",EDGE,{"disambiguationData":[OSD([sQuery(id+"F35.wireOp",EDGE,"E17.rect.top")])],"isStart":false});
            var Q22;
            {var subQ0=sQuery(id+"F35.wireOp",EDGE,"E18.left");var subQ1=sQuery(id+"F35.wireOp",EDGE,"E17.rect.right");var subQ2=sQuery(id+"F35.wireOp",EDGE,"E17.rect.top");Q22=makeQuery(id+"F38.boolean.opBoolean","SPLIT",EDGE,{"disambiguationData":[TD([makeQuery(id+"F36.opExtrude","SWEPT_FACE",FACE,{"disambiguationData":[OSD([subQ2])]})])],"derivedFrom":makeQuery(id+"F36.opExtrude","CAP_EDGE",EDGE,{"disambiguationData":[OSD([subQ1,subQ0])],"isStart":false})});}
            var Q23;
            Q23=makeQuery(id+"F38.boolean.opBoolean","MERGE",FACE,{"derivedFrom":[makeQuery(id+"F36.opExtrude","SWEPT_FACE",FACE,{"disambiguationData":[OSD([sQuery(id+"F35.wireOp",EDGE,"E17.rect.right"),sQuery(id+"F35.wireOp",EDGE,"E18.left")])]}),makeQuery(id+"F38.opExtrude","SWEPT_FACE",FACE,{"disambiguationData":[OSD([sQuery(id+"F37.wireOp",EDGE,"E19.right")])]})]});
            var Q24;
            Q24=makeQuery(id+"F38.opExtrude","CAP_EDGE",EDGE,{"disambiguationData":[OSD([sQuery(id+"F37.wireOp",EDGE,"E19.bottom")])],"isStart":false});
            var Q25;
            Q25=makeQuery(id+"F38.opExtrude","SWEPT_FACE",FACE,{"disambiguationData":[OSD([sQuery(id+"F37.wireOp",EDGE,"E19.left")])]});
            var Q26;
            Q26=makeQuery(id+"F38.opExtrude","CAP_EDGE",EDGE,{"disambiguationData":[OSD([sQuery(id+"F37.wireOp",EDGE,"E19.top")])],"isStart":false});
            var Q27;
            Q27=makeQuery(id+"F36.opExtrude","CAP_EDGE",EDGE,{"disambiguationData":[OSD([sQuery(id+"F35.wireOp",EDGE,"E17.rect.right"),sQuery(id+"F35.wireOp",EDGE,"E18.left")])],"isStart":true});
            var Q28;
            {var subQ0=sQuery(id+"F35.wireOp",EDGE,"E17.rect.left");Q28=makeQuery(id+"F36.opExtrude","CAP_EDGE",EDGE,{"disambiguationData":[OSD([subQ0]),TDD([makeQuery(id+"F35.imprint","IMPRINT",EDGE,{"disambiguationData":[TD([[makeQuery(id+"F35.imprint","INTERSECT",VERTEX,{"derivedFrom":[sQuery(id+"F35.wireOp",EDGE,"E17.rect.top"),subQ0]}),1.0]])],"derivedFrom":subQ0})])],"isStart":true});}
            var Q29;
            Q29=makeQuery(id+"F36.opExtrude","CAP_EDGE",EDGE,{"disambiguationData":[OSD([sQuery(id+"F35.wireOp",EDGE,"E18.right")])],"isStart":true});
            var Q30;
            Q30=makeQuery(id+"F36.opExtrude","CAP_EDGE",EDGE,{"disambiguationData":[OSD([sQuery(id+"F35.wireOp",EDGE,"E18.top")])],"isStart":true});
            var Q31;
            Q31=makeQuery(id+"F36.opExtrude","CAP_EDGE",EDGE,{"disambiguationData":[OSD([sQuery(id+"F35.wireOp",EDGE,"E18.bottom")])],"isStart":true});
            var Q32;
            Q32=makeQuery(id+"F36.opExtrude","CAP_EDGE",EDGE,{"disambiguationData":[OSD([sQuery(id+"F35.wireOp",EDGE,"E17.rect.bottom")])],"isStart":true});
            var Q33;
            Q33=makeQuery(id+"F36.opExtrude","CAP_EDGE",EDGE,{"disambiguationData":[OSD([sQuery(id+"F35.wireOp",EDGE,"E17.rect.top")])],"isStart":true});
            var Q34;
            {var subQ0=sQuery(id+"F35.wireOp",EDGE,"E17.rect.left");Q34=makeQuery(id+"F36.opExtrude","CAP_EDGE",EDGE,{"disambiguationData":[OSD([subQ0]),TDD([makeQuery(id+"F35.imprint","IMPRINT",EDGE,{"disambiguationData":[TD([[makeQuery(id+"F35.imprint","INTERSECT",VERTEX,{"derivedFrom":[sQuery(id+"F35.wireOp",EDGE,"E17.rect.bottom"),subQ0]}),-1.0]])],"derivedFrom":subQ0})])],"isStart":true});}
            var Q35;
            Q35=makeQuery(id+"F38.opExtrude","CAP_EDGE",EDGE,{"disambiguationData":[OSD([sQuery(id+"F37.wireOp",EDGE,"E19.right")])],"isStart":false});
            var Q36;
            Q36=makeQuery(id+"F38.opExtrude","CAP_EDGE",EDGE,{"disambiguationData":[OSD([sQuery(id+"F37.wireOp",EDGE,"E19.top")])],"isStart":true});
            var Q37;
            Q37=makeQuery(id+"F38.opExtrude","CAP_EDGE",EDGE,{"disambiguationData":[OSD([sQuery(id+"F37.wireOp",EDGE,"E19.bottom")])],"isStart":true});
            var Q38;
            Q38=makeQuery(id+"F38.opExtrude","CAP_EDGE",EDGE,{"disambiguationData":[OSD([sQuery(id+"F37.wireOp",EDGE,"E19.left")])],"isStart":false});
            var Q39;
            Q39=makeQuery(id+"F38.opExtrude","CAP_EDGE",EDGE,{"disambiguationData":[OSD([sQuery(id+"F37.wireOp",EDGE,"E19.left")])],"isStart":true});
            fillet(context, id + "F39", {"entities" : qUnion([Q0, Q1, Q2, Q3, Q4, Q5, Q6, Q7, Q8, Q9, Q10, Q11, Q12, Q13, Q14, Q15, Q16, Q17, Q18, Q19, Q20, Q21, Q22, Q23, Q24, Q25, Q26, Q27, Q28, Q29, Q30, Q31, Q32, Q33, Q34, Q35, Q36, Q37, Q38, Q39]), "radius" : 1.27 * mm, "tangentPropagation" : true, "allowEdgeOverflow" : false});
        }
    });
